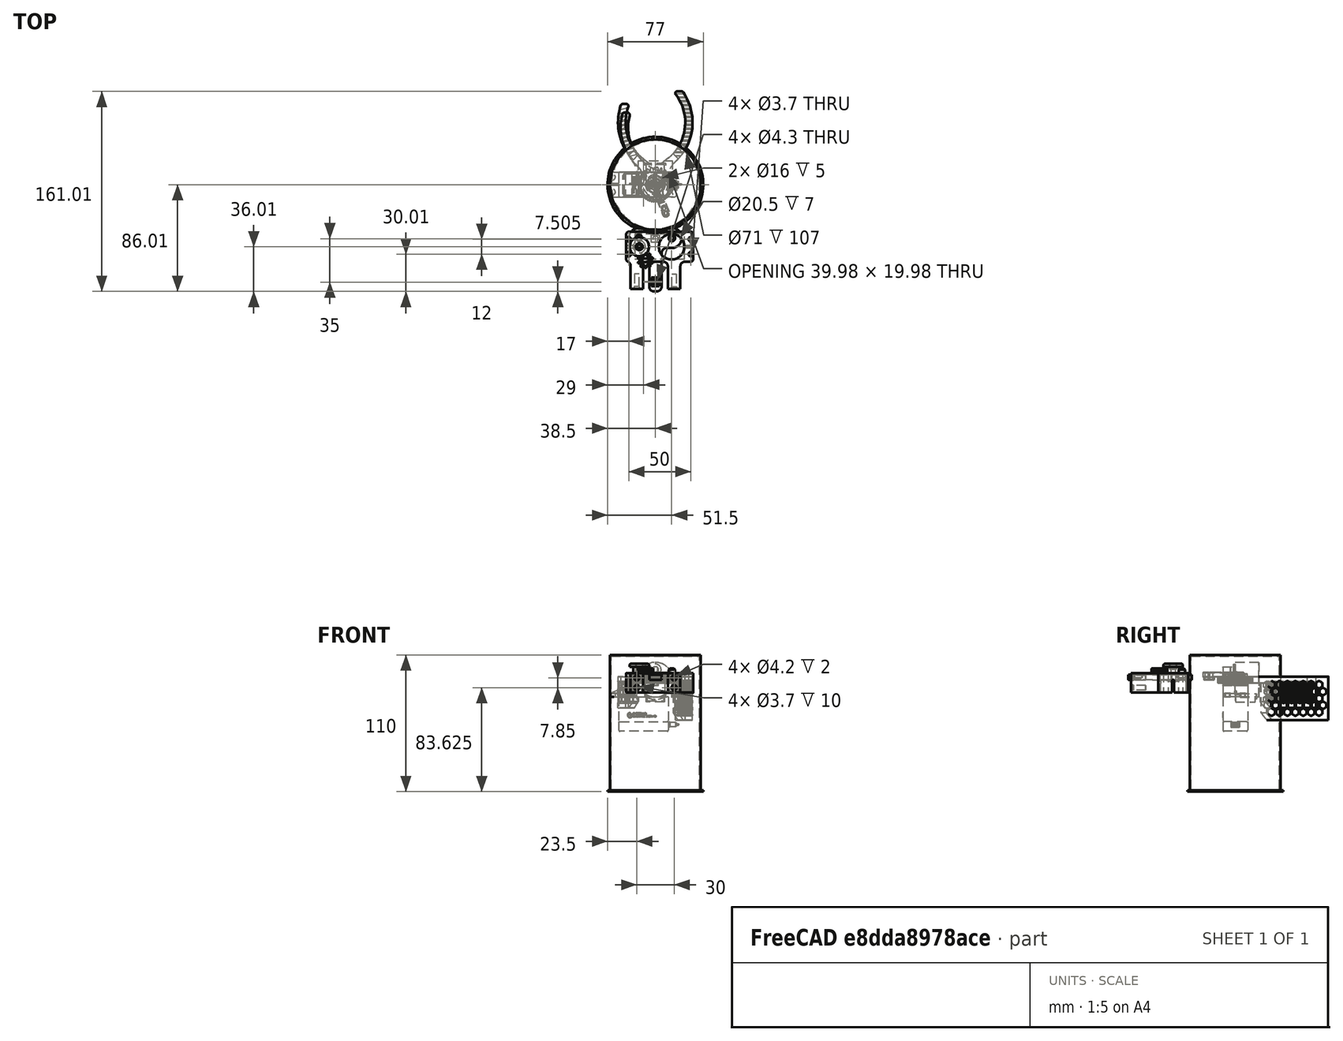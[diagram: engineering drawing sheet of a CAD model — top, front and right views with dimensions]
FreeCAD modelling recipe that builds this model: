
FCSTD DOCUMENT  (FreeCAD 1.0R39109 (Git))
Label: CanaPince
License: All rights reserved
LicenseURL: https://en.wikipedia.org/wiki/All_rights_reserved
objects: Sketcher::SketchObject×43, PartDesign::Pad×25, PartDesign::Pocket×20, PartDesign::CoordinateSystem×15, PartDesign::Body×12, PartDesign::Fillet×10, App::Part×8, PartDesign::Chamfer×6, Part::Part2DObjectPython×5, PartDesign::Mirrored×4, Part::Feature×3, Part::FeaturePython×3, PartDesign::Revolution×3, PartDesign::Line×2, Part::Cut×2, PartDesign::Plane×1, PartDesign::PolarPattern×1, Mesh::Feature×1, PartDesign::MultiTransform×1, App::VarSet×1
note: 333 computed .brp shape members not serialized (recipe doc carries the construction recipe); baked Part::Feature solids carry a one-line shape summary decoded from their .brp

FEATURE [Sketcher::SketchObject] Sketch
  ArcFitTolerance = 0
  AttachmentSupport = -> [XY_Plane]
  FullyConstrained = true
  MakeInternals = false
  MapMode = 5
  sketch-geometry (8):
    g0: ArcOfCircle CenterX=0 CenterY=0 CenterZ=0 NormalX=0 NormalY=0 NormalZ=1 AngleXU=0 Radius=37 StartAngle=4.41351 EndAngle=5.01126
    g1: ArcOfCircle CenterX=-13.25 CenterY=-43.0051 CenterZ=0 NormalX=0 NormalY=0 NormalZ=1 AngleXU=0 Radius=8 StartAngle=1.27192 EndAngle=4.71239
    g2: ArcOfCircle CenterX=13.25 CenterY=-43.0051 CenterZ=0 NormalX=0 NormalY=0 NormalZ=1 AngleXU=0 Radius=8 StartAngle=4.71239 EndAngle=8.15286
    g3: LineSegment StartX=-13.25 StartY=-51.0051 StartZ=0 EndX=-5 EndY=-51.0051 EndZ=0
    g4: LineSegment StartX=13.25 StartY=-51.0051 StartZ=0 EndX=5 EndY=-51.0051 EndZ=0
    g5: LineSegment StartX=-5 StartY=-51.0051 StartZ=0 EndX=-5 EndY=-86.0051 EndZ=0
    g6: LineSegment StartX=5 StartY=-51.0051 StartZ=0 EndX=5 EndY=-86.0051 EndZ=0
    g7: LineSegment StartX=-5 StartY=-86.0051 StartZ=0 EndX=5 EndY=-86.0051 EndZ=0
  constraints (24):
    c: Coincident(g0,g-1)
    c: Radius(g0) = 37
    c: Horizontal(g0,g0)
    c: Radius(g1) = 8
    c: Tangent(g1,g0) = 1.5708
    c: Radius(g2) = 8
    c: Distance(g1,g2) = 26.5
    c: Vertical(g1,g1)
    c: Vertical(g2,g2)
    c: Tangent(g2,g0) = 1.5708
    c: Coincident(g3,g1)
    c: Horizontal(g3)
    c: Coincident(g4,g2)
    c: Horizontal(g4)
    c: Equal(g3,g4)
    c: Distance(g3,g4) = 10
    c: Coincident(g5,g3)
    c: Vertical(g5)
    c: Distance(g5) = 35
    c: Coincident(g6,g4)
    c: Vertical(g6)
    c: Equal(g5,g6)
    c: Coincident(g7,g5)
    c: Coincident(g7,g6)
FEATURE [PartDesign::Pad] Pad
  Direction = (0,0,1)
  Length = 4
  Length2 = 10
  Profile = -> Sketch
  ReferenceAxis = -> Sketch [N_Axis]
  Suppressed = false
  Type = 0
FEATURE [Sketcher::SketchObject] Sketch001
  ArcFitTolerance = 0
  AttachmentSupport = -> [Pad]
  ExternalGeometry = -> [Pad]
  FullyConstrained = true
  MakeInternals = false
  MapMode = 5
  Placement = pos=(0,0,4) rot=(0,0,1;0rad)
  sketch-geometry (2):
    g0: Circle CenterX=-13.25 CenterY=-43.0051 CenterZ=0 NormalX=0 NormalY=0 NormalZ=1 AngleXU=0 Radius=2.6
    g1: Circle CenterX=13.25 CenterY=-43.0051 CenterZ=0 NormalX=0 NormalY=0 NormalZ=1 AngleXU=0 Radius=2.6
  constraints (4):
    c: Coincident(g0,g-3)
    c: Diameter(g0) = 5.2
    c: Coincident(g1,g-4)
    c: Equal(g1,g0)
FEATURE [PartDesign::Pad] Pad001
  BaseFeature = -> Pad
  Direction = (0,0,1)
  Length = 5
  Length2 = 10
  Profile = -> Sketch001
  ReferenceAxis = -> Sketch001 [N_Axis]
  Suppressed = false
  Type = 0
FEATURE [Sketcher::SketchObject] Sketch002
  ArcFitTolerance = 0
  AttachmentSupport = -> [Pad001]
  ExternalGeometry = -> [Pad001]
  FullyConstrained = true
  MakeInternals = false
  MapMode = 5
  Placement = pos=(0,0,4) rot=(0,0,1;0rad)
  sketch-geometry (2):
    g0: Circle CenterX=0 CenterY=-43.5051 CenterZ=0 NormalX=0 NormalY=0 NormalZ=1 AngleXU=0 Radius=2.15
    g1: Circle CenterX=0 CenterY=-78.0051 CenterZ=0 NormalX=0 NormalY=0 NormalZ=1 AngleXU=0 Radius=2.15
  constraints (6):
    c: PointOnObject(g0,g-2)
    c: Diameter(g0) = 4.3
    c: PointOnObject(g1,g-2)
    c: Equal(g0,g1)
    c: Distance(g0,g1) = 34.5
    c: Distance(g0,g-3) = 7.5
FEATURE [PartDesign::Pocket] Pocket
  BaseFeature = -> Pad001
  Direction = (0,0,-1)
  Length = 5
  Length2 = 5
  Profile = -> Sketch002
  ReferenceAxis = -> Sketch002 [N_Axis]
  Suppressed = false
  Type = 1
FEATURE [Sketcher::SketchObject] Sketch003
  ArcFitTolerance = 0
  AttachmentSupport = -> [Pocket]
  ExternalGeometry = -> [Pocket]
  FullyConstrained = true
  MakeInternals = false
  MapMode = 5
  Placement = pos=(0,0,4) rot=(0,0,1;0rad)
  sketch-geometry (10):
    g0: LineSegment StartX=-3.15 StartY=-46.6551 StartZ=0 EndX=-3.15 EndY=-40.3551 EndZ=0
    g1: LineSegment StartX=-3.15 StartY=-40.3551 StartZ=0 EndX=3.15 EndY=-40.3551 EndZ=0
    g2: LineSegment StartX=3.15 StartY=-40.3551 StartZ=0 EndX=3.15 EndY=-46.6551 EndZ=0
    g3: LineSegment StartX=3.15 StartY=-46.6551 StartZ=0 EndX=-3.15 EndY=-46.6551 EndZ=0
    g4: GeomPoint [constr] X=0 Y=-43.5051 Z=0
    g5: LineSegment StartX=-3.15 StartY=-81.1551 StartZ=0 EndX=-3.15 EndY=-74.8551 EndZ=0
    g6: LineSegment StartX=-3.15 StartY=-74.8551 StartZ=0 EndX=3.15 EndY=-74.8551 EndZ=0
    g7: LineSegment StartX=3.15 StartY=-74.8551 StartZ=0 EndX=3.15 EndY=-81.1551 EndZ=0
    g8: LineSegment StartX=3.15 StartY=-81.1551 StartZ=0 EndX=-3.15 EndY=-81.1551 EndZ=0
    g9: GeomPoint [constr] X=0 Y=-78.0051 Z=0
  constraints (24):
    c: Coincident(g0,g1)
    c: Coincident(g1,g2)
    c: Coincident(g2,g3)
    c: Coincident(g3,g0)
    c: Horizontal(g1)
    c: Horizontal(g3)
    c: Vertical(g0)
    c: Vertical(g2)
    c: Symmetric(g1,g0,g4)
    c: Coincident(g4,g-3)
    c: Distance(g1) = 6.3
    c: Equal(g1,g2)
    c: Coincident(g5,g6)
    c: Coincident(g6,g7)
    c: Coincident(g7,g8)
    c: Coincident(g8,g5)
    c: Horizontal(g6)
    c: Horizontal(g8)
    c: Vertical(g5)
    c: Vertical(g7)
    c: Symmetric(g6,g5,g9)
    c: Coincident(g9,g-4)
    c: Equal(g3,g6)
    c: Equal(g6,g7)
FEATURE [PartDesign::Pocket] Pocket001
  BaseFeature = -> Pocket
  Direction = (0,0,-1)
  Length = 2.5
  Length2 = 5
  Profile = -> Sketch003
  ReferenceAxis = -> Sketch003 [N_Axis]
  Suppressed = false
  Type = 0
FEATURE [PartDesign::Fillet] Fillet
  Base = -> Pocket001 [Edge34,Edge33,Edge35,Edge36]
  BaseFeature = -> Pocket001
  Radius = 4
  SupportTransform = false
  Suppressed = false
  UseAllEdges = false
FEATURE [PartDesign::Chamfer] Chamfer
  Angle = 45
  Base = -> Fillet [Edge66,Edge72]
  BaseFeature = -> Fillet
  ChamferType = 0
  FlipDirection = false
  Size = 1
  Size2 = 1
  SupportTransform = false
  Suppressed = false
  UseAllEdges = false
FEATURE [Sketcher::SketchObject] Sketch004
  ArcFitTolerance = 0
  AttachmentSupport = -> [Chamfer]
  ExternalGeometry = -> [Chamfer]
  FullyConstrained = true
  MakeInternals = false
  MapMode = 5
  Placement = pos=(0,0,4) rot=(0,0,1;0rad)
  sketch-geometry (1):
    g0: Circle CenterX=-7 CenterY=-60.7551 CenterZ=0 NormalX=0 NormalY=0 NormalZ=1 AngleXU=0 Radius=4.65
  constraints (3):
    c: Diameter(g0) = 9.3
    c: Distance(g0,g-3) = 2
    c: DistanceY(g0,g-4) = 17.25
FEATURE [PartDesign::Pocket] Pocket002
  BaseFeature = -> Chamfer
  Direction = (0,0,-1)
  Length = 5
  Length2 = 5
  Profile = -> Sketch004
  ReferenceAxis = -> Sketch004 [N_Axis]
  Suppressed = false
  Type = 1
FEATURE [PartDesign::Fillet] Fillet001
  Base = -> Pocket002 [Edge55,Edge52]
  BaseFeature = -> Pocket002
  Radius = 3
  SupportTransform = false
  Suppressed = false
  UseAllEdges = false
FEATURE [PartDesign::CoordinateSystem] LCS_1
  AttacherType = Attacher::AttachEngine3D
  AttachmentSupport = -> [Fillet001]
  MapMode = 11
  Placement = pos=(0,-43.5051,1.5) rot=(0,0,1;1.5708rad)
FEATURE [PartDesign::CoordinateSystem] LCS_2
  AttacherType = Attacher::AttachEngine3D
  AttachmentSupport = -> [Fillet001]
  MapMode = 11
  Placement = pos=(0,-78.0051,1.5) rot=(0,0,1;1.5708rad)
FEATURE [PartDesign::CoordinateSystem] LCS_3
  AttacherType = Attacher::AttachEngine3D
  AttachmentSupport = -> [Fillet001]
  MapMode = 11
  Placement = pos=(13.25,-43.0051,8) rot=(0,0,1;1.5708rad)
FEATURE [PartDesign::CoordinateSystem] LCS_4
  AttacherType = Attacher::AttachEngine3D
  AttachmentSupport = -> [Fillet001]
  MapMode = 11
  Placement = pos=(-13.25,-43.0051,8) rot=(0,0,1;1.5708rad)
FEATURE [PartDesign::Body] Body  label="partie_fixe_V1"
  AllowCompound = false
  Group = -> [Sketch,Pad,Sketch001,Pad001,Sketch002,Pocket,Sketch003,Pocket001,Fillet,Chamfer,Sketch004,Pocket002,Fillet001,LCS_1,LCS_2,LCS_3,LCS_4]
  Origin = -> Origin
  Tip = -> Fillet001
FEATURE [Part::Part2DObjectPython] InvoluteGear  # Draft 2D object (typed FeaturePython)
  AddendumCoefficient = 1
  DedendumCoefficient = 1.25
  ExternalGear = true
  HighPrecision = true
  Modules = 1
  NumberOfTeeth = 26
  Placement = pos=(-15,-46,0) rot=(0,0,20;0rad)
  PressureAngle = 20
  ProfileShiftCoefficient = 0
  RootFilletCoefficient = 0.38
FEATURE [Sketcher::SketchObject] Sketch005
  ArcFitTolerance = 0
  AttachmentSupport = -> [XY_Plane001]
  FullyConstrained = true
  MakeInternals = false
  MapMode = 5
  sketch-geometry (5):
    g0: ArcOfCircle CenterX=0 CenterY=0 CenterZ=0 NormalX=0 NormalY=0 NormalZ=1 AngleXU=0 Radius=37 StartAngle=2.8113 EndAngle=4.39717
    g1: Circle CenterX=-15 CenterY=-46 CenterZ=0 NormalX=0 NormalY=0 NormalZ=1 AngleXU=0 Radius=8
    g2: ArcOfCircle CenterX=-15 CenterY=-46 CenterZ=0 NormalX=0 NormalY=0 NormalZ=1 AngleXU=0 Radius=11.3839 StartAngle=2.22683 EndAngle=7.53877
    g3: ArcOfCircle CenterX=0 CenterY=0 CenterZ=0 NormalX=0 NormalY=0 NormalZ=1 AngleXU=0 Radius=43 StartAngle=2.85877 EndAngle=4.17683
    g4: LineSegment StartX=-41.2916 StartY=12 StartZ=0 EndX=-35 EndY=12 EndZ=0
  constraints (14):
    c: Coincident(g0,g-1)
    c: Radius(g0) = 37
    c: Distance(g0,g-2) = 35
    c: Diameter(g1) = 16
    c: Distance(g1,g-2) = 15
    c: Coincident(g2,g1)
    c: Tangent(g2,g0) = 1.5708
    c: Coincident(g3,g0)
    c: Coincident(g2,g3)
    c: Radius(g3) = 43
    c: Coincident(g4,g3)
    c: Coincident(g4,g0)
    c: Horizontal(g4)
    c: Distance(g1,g-1) = 46
FEATURE [PartDesign::Pad] Pad002
  Direction = (0,0,1)
  Length = 5
  Length2 = 10
  Midplane = true
  Profile = -> Sketch005
  ReferenceAxis = -> Sketch005 [N_Axis]
  Suppressed = false
  Type = 0
FEATURE [PartDesign::Fillet] Fillet002
  Base = -> Pad002 [Edge8]
  BaseFeature = -> Pad002
  Radius = 10
  SupportTransform = false
  Suppressed = false
  UseAllEdges = false
FEATURE [PartDesign::Fillet] Fillet003
  Base = -> Fillet002 [Edge17,Edge12]
  BaseFeature = -> Fillet002
  Radius = 2
  SupportTransform = false
  Suppressed = false
  UseAllEdges = false
FEATURE [PartDesign::Chamfer] Chamfer001
  Angle = 45
  Base = -> Fillet003 [Edge24,Edge8]
  BaseFeature = -> Fillet003
  ChamferType = 0
  FlipDirection = false
  Size = 0.8
  Size2 = 1
  SupportTransform = false
  Suppressed = false
  UseAllEdges = false
FEATURE [PartDesign::Line] DatumLine
  AttacherType = Attacher::AttachEngineLine
  AttachmentSupport = -> [Chamfer001]
  Length = 20
  MapMode = 42
  Placement = pos=(-15,-46,-1e-16) rot=(0,0,1;0rad)
  ResizeMode = 0
FEATURE [PartDesign::Pad] Pad003
  BaseFeature = -> Chamfer001
  Direction = (0,0,1)
  Length = 5
  Length2 = 10
  Midplane = true
  Profile = -> InvoluteGear
  ReferenceAxis = -> InvoluteGear [N_Axis]
  Suppressed = false
  Type = 0
FEATURE [Sketcher::SketchObject] Sketch006
  ArcFitTolerance = 0
  AttachmentSupport = -> [Pad003]
  FullyConstrained = false
  MakeInternals = false
  MapMode = 5
  Placement = pos=(0,0,2.5) rot=(0,0,1;0rad)
  sketch-geometry (1):
    g0: Circle CenterX=-15 CenterY=-46 CenterZ=0 NormalX=0 NormalY=0 NormalZ=1 AngleXU=0 Radius=8
  constraints (1):
    c: Diameter(g0) = 16
FEATURE [PartDesign::Pocket] Pocket003
  BaseFeature = -> Pad003
  Direction = (0,0,-1)
  Length = 5
  Length2 = 5
  Profile = -> Sketch006
  ReferenceAxis = -> Sketch006 [N_Axis]
  Suppressed = false
  Type = 1
FEATURE [Sketcher::SketchObject] Sketch007
  ArcFitTolerance = 0
  AttachmentSupport = -> [Pocket003]
  ExternalGeometry = -> [Pocket003]
  FullyConstrained = true
  MakeInternals = false
  MapMode = 5
  Placement = pos=(0,0,2.5) rot=(0,0,1;0rad)
  sketch-geometry (4):
    g0: ArcOfCircle CenterX=-15 CenterY=-46 CenterZ=0 NormalX=0 NormalY=0 NormalZ=1 AngleXU=0 Radius=11.5 StartAngle=0.593412 EndAngle=1.25558
    g1: ArcOfCircle CenterX=-15 CenterY=-46 CenterZ=0 NormalX=0 NormalY=0 NormalZ=1 AngleXU=0 Radius=15 StartAngle=0.593412 EndAngle=1.84626
    g2: LineSegment StartX=-5.46607 StartY=-39.5693 StartZ=0 EndX=-2.56444 EndY=-37.6121 EndZ=0
    g3: ArcOfCircle CenterX=0 CenterY=0 CenterZ=0 NormalX=0 NormalY=0 NormalZ=1 AngleXU=0 Radius=36.8839 StartAngle=4.1687 EndAngle=4.39717
  constraints (11):
    c: Coincident(g0,g-3)
    c: Coincident(g1,g0)
    c: Coincident(g2,g0)
    c: Coincident(g2,g1)
    c: Coincident(g1,g3)
    c: Tangent(g3,g0) = 1.5708
    c: Perpendicular(g0,g2)
    c: Radius(g0) = 11.5
    c: Coincident(g3,g-1)
    c: Radius(g1) = 15
    c: Angle(g-1,g2) = 0.593412
FEATURE [PartDesign::Pocket] Pocket004
  BaseFeature = -> Pocket003
  Direction = (0,0,-1)
  Length = 5
  Length2 = 5
  Profile = -> Sketch007
  ReferenceAxis = -> Sketch007 [N_Axis]
  Suppressed = false
  Type = 0
FEATURE [PartDesign::CoordinateSystem] LCS_005
  AttacherType = Attacher::AttachEngine3D
  AttachmentSupport = -> [Pocket004]
  MapMode = 11
  Placement = pos=(-15,-46,2.5) rot=(0,0,1;1.5708rad)
FEATURE [PartDesign::Body] Body001  label="bras_R"
  AllowCompound = false
  Group = -> [Sketch005,Pad002,Fillet002,Fillet003,Chamfer001,DatumLine,InvoluteGear,Pad003,Sketch006,Pocket003,Sketch007,Pocket004,LCS_005]
  Origin = -> Origin001
  Placement = pos=(15,46,0) rot=(0,0,1;0rad)
  Tip = -> Pocket004
FEATURE [Part::Part2DObjectPython] InvoluteGear001  # Draft 2D object (typed FeaturePython)
  AddendumCoefficient = 1
  DedendumCoefficient = 1.25
  ExternalGear = true
  HighPrecision = true
  Modules = 1.05
  NumberOfTeeth = 10
  PressureAngle = 20
  ProfileShiftCoefficient = 0
  RootFilletCoefficient = 0.38
FEATURE [PartDesign::Pad] Pad004
  Direction = (0,0,1)
  Length = 4
  Length2 = 10
  Profile = -> InvoluteGear001
  ReferenceAxis = -> InvoluteGear001 [N_Axis]
  Suppressed = false
  Type = 0
FEATURE [Sketcher::SketchObject] Sketch008
  ArcFitTolerance = 0
  AttachmentSupport = -> [XY_Plane002]
  FullyConstrained = true
  MakeInternals = false
  MapMode = 5
  sketch-geometry (1):
    g0: Circle CenterX=0 CenterY=0 CenterZ=0 NormalX=0 NormalY=0 NormalZ=1 AngleXU=0 Radius=6.5
  constraints (2):
    c: Coincident(g0,g-1)
    c: Diameter(g0) = 13
FEATURE [Sketcher::SketchObject] Sketch009
  ArcFitTolerance = 0
  AttachmentSupport = -> [Pad004]
  FullyConstrained = true
  MakeInternals = false
  MapMode = 5
  Placement = pos=(0,0,4) rot=(0,0,1;0rad)
  sketch-geometry (5):
    g0: LineSegment StartX=-1.5 StartY=-2.5 StartZ=0 EndX=-1.5 EndY=2.5 EndZ=0
    g1: LineSegment StartX=-1.5 StartY=2.5 StartZ=0 EndX=1.5 EndY=2.5 EndZ=0
    g2: LineSegment StartX=1.5 StartY=2.5 StartZ=0 EndX=1.5 EndY=-2.5 EndZ=0
    g3: LineSegment StartX=1.5 StartY=-2.5 StartZ=0 EndX=-1.5 EndY=-2.5 EndZ=0
    g4: GeomPoint [constr] X=0 Y=0 Z=0
  constraints (12):
    c: Coincident(g0,g1)
    c: Coincident(g1,g2)
    c: Coincident(g2,g3)
    c: Coincident(g3,g0)
    c: Horizontal(g1)
    c: Horizontal(g3)
    c: Vertical(g0)
    c: Vertical(g2)
    c: Symmetric(g1,g0,g4)
    c: Coincident(g4,g-1)
    c: Distance(g2) = 5
    c: Distance(g1) = 3
FEATURE [PartDesign::Pocket] Pocket005
  BaseFeature = -> Pad004
  Direction = (0,0,-1)
  Length = 5
  Length2 = 5
  Profile = -> Sketch009
  ReferenceAxis = -> Sketch009 [N_Axis]
  Suppressed = false
  Type = 1
FEATURE [PartDesign::Fillet] Fillet004
  Base = -> Pocket005 [Edge310,Edge311,Edge312,Edge309]
  BaseFeature = -> Pocket005
  Radius = 0.8
  SupportTransform = false
  Suppressed = false
  UseAllEdges = false
FEATURE [PartDesign::CoordinateSystem] LCS_006
  AttacherType = Attacher::AttachEngine3D
  AttachmentSupport = -> [Fillet004]
  MapMode = 5
  Placement = pos=(0,0,4) rot=(0,0,1;0rad)
FEATURE [PartDesign::Body] Body002  label="pignon"
  AllowCompound = false
  Group = -> [Sketch008,InvoluteGear001,Pad004,Sketch009,Pocket005,Fillet004,LCS_006]
  Origin = -> Origin002
  Placement = pos=(-8,-61,5) rot=(0,0,1;4.71239rad)
  Tip = -> Fillet004
FEATURE [Sketcher::SketchObject] Sketch010
  ArcFitTolerance = 0
  AttachmentSupport = -> [XZ_Plane004]
  FullyConstrained = true
  MakeInternals = false
  MapMode = 5
  Placement = pos=(0,0,0) rot=(1,0,0;1.5708rad)
  sketch-geometry (1):
    g0: Circle CenterX=0 CenterY=0 CenterZ=0 NormalX=0 NormalY=0 NormalZ=1 AngleXU=0 Radius=14
  constraints (2):
    c: Coincident(g0,g-1)
    c: Diameter(g0) = 28
FEATURE [PartDesign::Pad] Pad005
  Direction = (0,-1,2e-16)
  Length = 19
  Length2 = 100
  Placement = pos=(0,0,0) rot=(1,0,0;1.5708rad)
  Profile = -> Sketch010
  ReferenceAxis = -> Sketch010 [N_Axis]
  Reversed = true
  Suppressed = false
  Type = 0
FEATURE [Sketcher::SketchObject] Sketch011
  ArcFitTolerance = 0
  AttachmentSupport = -> [Pad005]
  ExternalGeometry = -> [Pad005]
  FullyConstrained = true
  MakeInternals = false
  MapMode = 5
  Placement = pos=(0,0,0) rot=(1,0,0;1.5708rad)
  sketch-geometry (4):
    g0: LineSegment StartX=-7.25 StartY=-11.9765 StartZ=0 EndX=7.25 EndY=-11.9765 EndZ=0
    g1: LineSegment StartX=7.25 StartY=-11.9765 StartZ=0 EndX=7.25 EndY=-18 EndZ=0
    g2: LineSegment StartX=7.25 StartY=-18 StartZ=0 EndX=-7.25 EndY=-18 EndZ=0
    g3: LineSegment StartX=-7.25 StartY=-18 StartZ=0 EndX=-7.25 EndY=-11.9765 EndZ=0
  constraints (11):
    c: Coincident(g0,g1)
    c: Coincident(g1,g2)
    c: Coincident(g2,g3)
    c: Coincident(g3,g0)
    c: Horizontal(g0)
    c: Vertical(g1)
    c: Vertical(g3)
    c: PointOnObject(g0,g-3)
    c: Symmetric(g2,g1,g-2)
    c: DistanceX(g2,g2) = 14.5
    c: DistanceY(g1,g-1) = 18
FEATURE [PartDesign::Pad] Pad006
  BaseFeature = -> Pad005
  Direction = (0,-1,2e-16)
  Length = 16
  Length2 = 100
  Placement = pos=(0,0,0) rot=(1,0,0;1.5708rad)
  Profile = -> Sketch011
  ReferenceAxis = -> Sketch011 [N_Axis]
  Refine = true
  Reversed = true
  Suppressed = false
  Type = 0
FEATURE [Sketcher::SketchObject] Sketch012
  ArcFitTolerance = 0
  AttachmentSupport = -> [Pad006]
  ExternalGeometry = -> [Pad006]
  FullyConstrained = true
  MakeInternals = false
  MapMode = 5
  Placement = pos=(0,0,0) rot=(1,0,0;1.5708rad)
  sketch-geometry (5):
    g0: Circle CenterX=-17.5 CenterY=-1e-16 CenterZ=0 NormalX=0 NormalY=0 NormalZ=1 AngleXU=0 Radius=2.1
    g1: ArcOfCircle CenterX=-17.5 CenterY=-1e-16 CenterZ=0 NormalX=0 NormalY=0 NormalZ=1 AngleXU=0 Radius=3.5 StartAngle=1.5708 EndAngle=4.71239
    g2: LineSegment StartX=-17.5 StartY=3.5 StartZ=0 EndX=-13.5554 EndY=3.5 EndZ=0
    g3: LineSegment StartX=-13.5554 StartY=3.5 StartZ=0 EndX=-13.5554 EndY=-3.5 EndZ=0
    g4: LineSegment StartX=-13.5554 StartY=-3.5 StartZ=0 EndX=-17.5 EndY=-3.5 EndZ=0
  constraints (14):
    c: Coincident(g1,g0)
    c: Symmetric(g1,g1,g-1)
    c: Vertical(g1,g0)
    c: Coincident(g2,g1)
    c: Horizontal(g2)
    c: Coincident(g3,g2)
    c: Vertical(g3)
    c: Coincident(g4,g3)
    c: Coincident(g4,g1)
    c: Horizontal(g4)
    c: PointOnObject(g2,g-3)
    c: Diameter(g0) = 4.2
    c: Radius(g1) = 3.5
    c: DistanceX(g0,g-1) = 17.5
FEATURE [PartDesign::Pad] Pad007
  BaseFeature = -> Pad006
  Direction = (0,-1,2e-16)
  Length = 0.8
  Length2 = 100
  Placement = pos=(0,0,0) rot=(1,0,0;1.5708rad)
  Profile = -> Sketch012
  ReferenceAxis = -> Sketch012 [N_Axis]
  Refine = true
  Reversed = true
  Suppressed = false
  Type = 0
FEATURE [PartDesign::Mirrored] Mirrored
  BaseFeature = -> Pad007
  MirrorPlane = -> Sketch012 [V_Axis]
  Originals = -> [Pad007]
  Placement = pos=(0,0,0) rot=(1,0,0;1.5708rad)
  Refine = true
  Suppressed = false
  TransformMode = 0
FEATURE [Sketcher::SketchObject] Sketch013
  ArcFitTolerance = 0
  AttachmentSupport = -> [Mirrored]
  FullyConstrained = true
  MakeInternals = false
  MapMode = 5
  Placement = pos=(0,0,0) rot=(1,0,0;1.5708rad)
  sketch-geometry (1):
    g0: Circle CenterX=0 CenterY=8 CenterZ=0 NormalX=0 NormalY=0 NormalZ=1 AngleXU=0 Radius=4.6
  constraints (3):
    c: PointOnObject(g0,g-2)
    c: Diameter(g0) = 9.2
    c: DistanceY(g-1,g0) = 8
FEATURE [PartDesign::Pad] Pad008
  BaseFeature = -> Mirrored
  Direction = (0,-1,2e-16)
  Length = 1.5
  Length2 = 100
  Placement = pos=(0,0,0) rot=(1,0,0;1.5708rad)
  Profile = -> Sketch013
  ReferenceAxis = -> Sketch013 [N_Axis]
  Suppressed = false
  Type = 0
FEATURE [Sketcher::SketchObject] Sketch014
  ArcFitTolerance = 0
  AttachmentSupport = -> [Pad008]
  ExternalGeometry = -> [Pad008]
  FullyConstrained = true
  MakeInternals = false
  MapMode = 5
  Placement = pos=(0,-1.5,0) rot=(1,0,0;1.5708rad)
  sketch-geometry (1):
    g0: Circle CenterX=0 CenterY=8 CenterZ=0 NormalX=0 NormalY=0 NormalZ=1 AngleXU=0 Radius=2.5
  constraints (2):
    c: Coincident(g0,g-3)
    c: Diameter(g0) = 5
FEATURE [PartDesign::Pad] Pad009
  BaseFeature = -> Pad008
  Direction = (0,-1,2e-16)
  Length = 2.5
  Length2 = 100
  Placement = pos=(0,0,0) rot=(1,0,0;1.5708rad)
  Profile = -> Sketch014
  ReferenceAxis = -> Sketch014 [N_Axis]
  Suppressed = false
  Type = 0
FEATURE [Sketcher::SketchObject] Sketch015
  ArcFitTolerance = 0
  AttachmentSupport = -> [Pad009]
  ExternalGeometry = -> [Pad009]
  FullyConstrained = true
  MakeInternals = false
  MapMode = 5
  Placement = pos=(0,-4,0) rot=(1,0,0;1.5708rad)
  sketch-geometry (4):
    g0: LineSegment StartX=-1.5 StartY=10 StartZ=0 EndX=-1.5 EndY=6 EndZ=0
    g1: LineSegment StartX=1.5 StartY=10 StartZ=0 EndX=1.5 EndY=6 EndZ=0
    g2: ArcOfCircle CenterX=0 CenterY=8 CenterZ=0 NormalX=0 NormalY=0 NormalZ=1 AngleXU=0 Radius=2.5 StartAngle=0.927295 EndAngle=2.2143
    g3: ArcOfCircle CenterX=0 CenterY=8 CenterZ=0 NormalX=0 NormalY=0 NormalZ=1 AngleXU=0 Radius=2.5 StartAngle=4.06889 EndAngle=5.35589
  constraints (12):
    c: PointOnObject(g0,g-3)
    c: PointOnObject(g0,g-3)
    c: Vertical(g0)
    c: Vertical(g1)
    c: Coincident(g2,g-3)
    c: Coincident(g2,g0)
    c: Coincident(g2,g1)
    c: Coincident(g3,g2)
    c: Coincident(g3,g0)
    c: Coincident(g3,g1)
    c: DistanceX(g0,g1) = 3
    c: Horizontal(g0,g1)
FEATURE [PartDesign::Pad] Pad010
  BaseFeature = -> Pad009
  Direction = (0,-1,2e-16)
  Length = 6
  Length2 = 100
  Placement = pos=(0,0,0) rot=(1,0,0;1.5708rad)
  Profile = -> Sketch015
  ReferenceAxis = -> Sketch015 [N_Axis]
  Refine = true
  Suppressed = false
  Type = 0
FEATURE [PartDesign::Plane] DatumPlane
  AttachmentOffset = pos=(0,0,-4) rot=(0,0,1;0rad)
  AttachmentSupport = -> [Pad010]
  Length = 60
  MapMode = 2
  Placement = pos=(0,4,-9e-16) rot=(1,0,0;1.5708rad)
  ResizeMode = 0
  Width = 60
FEATURE [Sketcher::SketchObject] Sketch016
  ArcFitTolerance = 0
  AttachmentSupport = -> [DatumPlane]
  ExternalGeometry = -> [Pad010]
  FullyConstrained = true
  MakeInternals = false
  MapMode = 5
  Placement = pos=(0,4,-9e-16) rot=(1,0,0;1.5708rad)
  sketch-geometry (4):
    g0: ArcOfCircle CenterX=0 CenterY=0 CenterZ=0 NormalX=0 NormalY=0 NormalZ=1 AngleXU=0 Radius=15.7659 StartAngle=4.14297 EndAngle=4.23456
    g1: LineSegment StartX=-7.25 StartY=-14 StartZ=0 EndX=-7.25 EndY=-11.9765 EndZ=0
    g2: LineSegment StartX=-8.5 StartY=-13.2783 StartZ=0 EndX=-8.5 EndY=-11.1243 EndZ=0
    g3: ArcOfCircle CenterX=0 CenterY=0 CenterZ=0 NormalX=0 NormalY=0 NormalZ=1 AngleXU=0 Radius=14 StartAngle=4.05993 EndAngle=4.16804
  constraints (11):
    c: Coincident(g0,g-1)
    c: Coincident(g1,g-4)
    c: Coincident(g2,g0)
    c: Vertical(g2)
    c: Coincident(g3,g0)
    c: Coincident(g3,g1)
    c: Coincident(g3,g2)
    c: Coincident(g1,g0)
    c: DistanceX(g2,g0) = 8.5
    c: Vertical(g1)
    c: DistanceY(g-3,g0) = 4
FEATURE [PartDesign::Pad] Pad011
  BaseFeature = -> Pad010
  Direction = (0,-1,2e-16)
  Length = 10
  Length2 = 100
  Placement = pos=(0,0,0) rot=(1,0,0;1.5708rad)
  Profile = -> Sketch016
  ReferenceAxis = -> Sketch016 [N_Axis]
  Refine = true
  Suppressed = false
  Type = 3
  UpToFace = -> Pad010 [Face11]
FEATURE [PartDesign::Mirrored] Mirrored001
  BaseFeature = -> Pad011
  MirrorPlane = -> Sketch016 [V_Axis]
  Originals = -> [Pad011]
  Placement = pos=(0,0,0) rot=(1,0,0;1.5708rad)
  Refine = true
  Suppressed = false
  TransformMode = 0
FEATURE [Sketcher::SketchObject] Sketch017
  ArcFitTolerance = 0
  AttachmentSupport = -> [Mirrored001]
  ExternalGeometry = -> [Mirrored001]
  FullyConstrained = true
  MakeInternals = false
  MapMode = 5
  Placement = pos=(0,16,0) rot=(-1,0,0;1.5708rad)
  sketch-geometry (4):
    g0: ArcOfCircle CenterX=0 CenterY=0 CenterZ=0 NormalX=0 NormalY=0 NormalZ=1 AngleXU=0 Radius=14 StartAngle=0.918336 EndAngle=2.22326
    g1: ArcOfCircle CenterX=0 CenterY=0 CenterZ=0 NormalX=0 NormalY=0 NormalZ=1 AngleXU=0 Radius=15.7659 StartAngle=1.00138 EndAngle=2.14021
    g2: LineSegment StartX=-8.5 StartY=13.2783 StartZ=0 EndX=-8.5 EndY=11.1243 EndZ=0
    g3: LineSegment StartX=8.5 StartY=13.2783 StartZ=0 EndX=8.5 EndY=11.1243 EndZ=0
  constraints (10):
    c: Coincident(g0,g-1)
    c: Coincident(g0,g-3)
    c: Coincident(g1,g0)
    c: Coincident(g1,g-4)
    c: Coincident(g2,g1)
    c: Coincident(g2,g0)
    c: Coincident(g3,g1)
    c: Coincident(g3,g0)
    c: Vertical(g3)
    c: Horizontal(g1,g1)
FEATURE [PartDesign::Pad] Pad012
  BaseFeature = -> Mirrored001
  Direction = (0,1,2e-16)
  Length = 1
  Length2 = 100
  Placement = pos=(0,0,0) rot=(1,0,0;1.5708rad)
  Profile = -> Sketch017
  ReferenceAxis = -> Sketch017 [N_Axis]
  Refine = true
  Suppressed = false
  Type = 0
FEATURE [Sketcher::SketchObject] Sketch018
  ArcFitTolerance = 0
  AttachmentSupport = -> [Pad012]
  ExternalGeometry = -> [Pad012]
  FullyConstrained = false
  MakeInternals = false
  MapMode = 5
  Placement = pos=(0,0,0) rot=(1,0,0;1.5708rad)
  sketch-geometry (8):
    g0: LineSegment StartX=-7.25 StartY=-11.9765 StartZ=0 EndX=-7.25 EndY=-18 EndZ=0
    g1: LineSegment StartX=7.25 StartY=-18 StartZ=0 EndX=-7.25 EndY=-18 EndZ=0
    g2: LineSegment StartX=7.25 StartY=-18 StartZ=0 EndX=7.25 EndY=-11.9765 EndZ=0
    g3: ArcOfCircle CenterX=0 CenterY=0 CenterZ=0 NormalX=0 NormalY=0 NormalZ=1 AngleXU=0 Radius=14 StartAngle=4.16804 EndAngle=4.20929
    g4: LineSegment StartX=-6.75 StartY=-12.2653 StartZ=0 EndX=-6.75 EndY=-17 EndZ=0
    g5: LineSegment StartX=-6.75 StartY=-17 StartZ=0 EndX=6.75 EndY=-17 EndZ=0
    g6: LineSegment StartX=6.75 StartY=-17 StartZ=0 EndX=6.75 EndY=-12.2653 EndZ=0
    g7: ArcOfCircle CenterX=-1.15416 CenterY=1.9985 CenterZ=0 NormalX=0 NormalY=0 NormalZ=1 AngleXU=0 Radius=16.3074 StartAngle=5.21841 EndAngle=5.25381
  constraints (19):
    c: Coincident(g0,g-3)
    c: Coincident(g0,g-5)
    c: Coincident(g1,g-6)
    c: Coincident(g1,g0)
    c: Coincident(g2,g1)
    c: Coincident(g2,g-4)
    c: Coincident(g3,g-1)
    c: Coincident(g3,g0)
    c: Coincident(g7,g2)
    c: Vertical(g4)
    c: Coincident(g5,g4)
    c: Horizontal(g5)
    c: Coincident(g6,g5)
    c: Symmetric(g4,g6,g-2)
    c: Vertical(g6)
    c: DistanceX(g0,g4) = 0.5
    c: DistanceY(g0,g4) = 1
    c: Coincident(g3,g4)
    c: Coincident(g7,g6)
FEATURE [PartDesign::Pocket] Pocket006
  BaseFeature = -> Pad012
  Direction = (0,1,-2e-16)
  Length = 0.1
  Length2 = 100
  Placement = pos=(0,0,0) rot=(1,0,0;1.5708rad)
  Profile = -> Sketch018
  Suppressed = false
  Type = 0
FEATURE [PartDesign::Body] Body003  label="28BYJ_48_StepperBody"
  AllowCompound = false
  Group = -> [Sketch010,Pad005,Sketch011,Pad006,Sketch012,Pad007,Mirrored,Sketch013,Pad008,Sketch014,Pad009,Sketch015,Pad010,DatumPlane,Sketch016,Pad011,Mirrored001,Sketch017,Pad012,Sketch018,Pocket006]
  Origin = -> Origin004
  Tip = -> Pocket006
FEATURE [PartDesign::CoordinateSystem] LCS_Mounting_Hole1
  AttacherType = Attacher::AttachEngine3D
  AttachmentSupport = -> [Pocket006]
  MapMode = 11
  Placement = pos=(-17.5,0.8,-1e-16) rot=(0.57735,-0.57735,0.57735;2.0944rad)
FEATURE [PartDesign::CoordinateSystem] LCS_Mounting_Hole2
  AttacherType = Attacher::AttachEngine3D
  AttachmentOffset = pos=(0,0,0) rot=(1,0,0;3.14159rad)
  AttachmentSupport = -> [Pocket006]
  MapMode = 11
  Placement = pos=(17.5,0.8,-1e-16) rot=(-0.57735,0.57735,-0.57735;4.18879rad)
FEATURE [PartDesign::CoordinateSystem] LCS_Mounting_Housing_Center
  AttacherType = Attacher::AttachEngine3D
  AttachmentSupport = -> [Pocket006]
  MapMode = 11
  Placement = pos=(0,0.8,-4e-16) rot=(0.480384,0.620174,-0.620174;2.24593rad)
FEATURE [PartDesign::CoordinateSystem] LCS_Shaft_top_center
  AttacherType = Attacher::AttachEngine3D
  AttachmentOffset = pos=(0,0,8.5) rot=(0,0,1;0rad)
  AttachmentSupport = -> [Pocket006]
  MapMode = 11
  Placement = pos=(0,-10,8) rot=(0.57735,-0.57735,0.57735;2.0944rad)
FEATURE [App::Part] Part  label="28BYJ_48"
  Group = -> [Body003,LCS_Mounting_Housing_Center,LCS_Shaft_top_center,LCS_Mounting_Hole1,LCS_Mounting_Hole2]
  Origin = -> Origin003
  Placement = pos=(-2.03e-14,-61,1.02e-14) rot=(-0.57735,-0.57735,0.57735;2.0944rad)
FEATURE [Part::Part2DObjectPython] InvoluteGear002  # Draft 2D object (typed FeaturePython)
  AddendumCoefficient = 1
  DedendumCoefficient = 1.25
  ExternalGear = true
  HighPrecision = true
  Modules = 1
  NumberOfTeeth = 26
  Placement = pos=(-15,-46,0) rot=(0,0,1;0.122173rad)
  PressureAngle = 20
  ProfileShiftCoefficient = 0
  RootFilletCoefficient = 0.38
FEATURE [Sketcher::SketchObject] Sketch019
  ArcFitTolerance = 0
  AttachmentSupport = -> [XY_Plane005]
  FullyConstrained = true
  MakeInternals = false
  MapMode = 5
  sketch-geometry (5):
    g0: ArcOfCircle CenterX=0 CenterY=0 CenterZ=0 NormalX=0 NormalY=0 NormalZ=1 AngleXU=0 Radius=37 StartAngle=2.8113 EndAngle=4.39717
    g1: Circle CenterX=-15 CenterY=-46 CenterZ=0 NormalX=0 NormalY=0 NormalZ=1 AngleXU=0 Radius=8
    g2: ArcOfCircle CenterX=-15 CenterY=-46 CenterZ=0 NormalX=0 NormalY=0 NormalZ=1 AngleXU=0 Radius=11.3839 StartAngle=2.22683 EndAngle=7.53877
    g3: ArcOfCircle CenterX=0 CenterY=0 CenterZ=0 NormalX=0 NormalY=0 NormalZ=1 AngleXU=0 Radius=43 StartAngle=2.85877 EndAngle=4.17683
    g4: LineSegment StartX=-41.2916 StartY=12 StartZ=0 EndX=-35 EndY=12 EndZ=0
  constraints (14):
    c: Coincident(g0,g-1)
    c: Radius(g0) = 37
    c: Distance(g0,g-2) = 35
    c: Diameter(g1) = 16
    c: Distance(g1,g-2) = 15
    c: Coincident(g2,g1)
    c: Tangent(g2,g0) = 1.5708
    c: Coincident(g3,g0)
    c: Coincident(g2,g3)
    c: Radius(g3) = 43
    c: Coincident(g4,g3)
    c: Coincident(g4,g0)
    c: Horizontal(g4)
    c: Distance(g1,g-1) = 46
FEATURE [PartDesign::Pad] Pad013
  Direction = (0,0,1)
  Length = 5
  Length2 = 10
  Midplane = true
  Profile = -> Sketch019
  ReferenceAxis = -> Sketch019 [N_Axis]
  Suppressed = false
  Type = 0
FEATURE [PartDesign::Fillet] Fillet005
  Base = -> Pad013 [Edge8]
  BaseFeature = -> Pad013
  Radius = 10
  SupportTransform = false
  Suppressed = false
  UseAllEdges = false
FEATURE [PartDesign::Fillet] Fillet006
  Base = -> Fillet005 [Edge17,Edge12]
  BaseFeature = -> Fillet005
  Radius = 2
  SupportTransform = false
  Suppressed = false
  UseAllEdges = false
FEATURE [PartDesign::Chamfer] Chamfer002
  Angle = 45
  Base = -> Fillet006 [Edge24,Edge8]
  BaseFeature = -> Fillet006
  ChamferType = 0
  FlipDirection = false
  Size = 0.8
  Size2 = 1
  SupportTransform = false
  Suppressed = false
  UseAllEdges = false
FEATURE [PartDesign::Line] DatumLine001
  AttacherType = Attacher::AttachEngineLine
  AttachmentSupport = -> [Chamfer002]
  Length = 20
  MapMode = 42
  Placement = pos=(-15,-46,-1e-16) rot=(0,0,1;0rad)
  ResizeMode = 0
FEATURE [PartDesign::Pad] Pad014
  BaseFeature = -> Chamfer002
  Direction = (0,0,1)
  Length = 5
  Length2 = 10
  Midplane = true
  Profile = -> InvoluteGear002
  ReferenceAxis = -> InvoluteGear002 [N_Axis]
  Suppressed = false
  Type = 0
FEATURE [Sketcher::SketchObject] Sketch020
  ArcFitTolerance = 0
  AttachmentSupport = -> [Pad014]
  FullyConstrained = false
  MakeInternals = false
  MapMode = 5
  Placement = pos=(0,0,2.5) rot=(0,0,1;0rad)
  sketch-geometry (1):
    g0: Circle CenterX=-15 CenterY=-46 CenterZ=0 NormalX=0 NormalY=0 NormalZ=1 AngleXU=0 Radius=8
  constraints (1):
    c: Diameter(g0) = 16
FEATURE [PartDesign::Pocket] Pocket007
  BaseFeature = -> Pad014
  Direction = (0,0,-1)
  Length = 5
  Length2 = 5
  Profile = -> Sketch020
  ReferenceAxis = -> Sketch020 [N_Axis]
  Suppressed = false
  Type = 1
FEATURE [Sketcher::SketchObject] Sketch021
  ArcFitTolerance = 0
  AttachmentSupport = -> [Pocket007]
  ExternalGeometry = -> [Pocket007]
  FullyConstrained = true
  MakeInternals = false
  MapMode = 5
  Placement = pos=(0,0,2.5) rot=(0,0,1;0rad)
  sketch-geometry (4):
    g0: ArcOfCircle CenterX=-15 CenterY=-46 CenterZ=0 NormalX=0 NormalY=0 NormalZ=1 AngleXU=0 Radius=11.4 StartAngle=0.488692 EndAngle=1.25558
    g1: ArcOfCircle CenterX=0 CenterY=0 CenterZ=0 NormalX=0 NormalY=0 NormalZ=1 AngleXU=0 Radius=36.9839 StartAngle=4.1662 EndAngle=4.39717
    g2: ArcOfCircle CenterX=-15 CenterY=-46 CenterZ=0 NormalX=0 NormalY=0 NormalZ=1 AngleXU=0 Radius=15 StartAngle=0.488692 EndAngle=1.85533
    g3: LineSegment StartX=-4.9344 StartY=-40.648 StartZ=0 EndX=-1.75579 EndY=-38.9579 EndZ=0
  constraints (11):
    c: Coincident(g1,g-1)
    c: Coincident(g2,g0)
    c: Coincident(g2,g1)
    c: Coincident(g3,g0)
    c: Coincident(g3,g2)
    c: Radius(g0) = 11.4
    c: Tangent(g1,g0) = 1.5708
    c: Coincident(g0,g-3)
    c: Radius(g2) = 15
    c: Perpendicular(g0,g3)
    c: Angle(g-1,g3) = 0.488692
FEATURE [PartDesign::Pocket] Pocket008
  BaseFeature = -> Pocket007
  Direction = (0,0,-1)
  Length = 5
  Length2 = 5
  Profile = -> Sketch021
  ReferenceAxis = -> Sketch021 [N_Axis]
  Suppressed = false
  Type = 0
FEATURE [PartDesign::CoordinateSystem] LCS_007
  AttacherType = Attacher::AttachEngine3D
  AttachmentSupport = -> [Pocket008]
  MapMode = 11
  Placement = pos=(-15,-46,2.5) rot=(0,0,1;1.5708rad)
FEATURE [PartDesign::Body] Body004  label="bras_L"
  AllowCompound = false
  Group = -> [Sketch019,Pad013,Fillet005,Fillet006,Chamfer002,DatumLine001,InvoluteGear002,Pad014,Sketch020,Pocket007,Sketch021,Pocket008,LCS_007]
  Origin = -> Origin005
  Placement = pos=(15,46,0) rot=(0,0,1;0rad)
  Tip = -> Pocket008
FEATURE [Sketcher::SketchObject] Sketch022
  ArcFitTolerance = 0
  AttachmentSupport = -> [XY_Plane006]
  FullyConstrained = true
  MakeInternals = false
  MapMode = 5
  sketch-geometry (8):
    g0: ArcOfCircle CenterX=0 CenterY=0 CenterZ=0 NormalX=0 NormalY=0 NormalZ=1 AngleXU=0 Radius=37 StartAngle=4.41351 EndAngle=5.01126
    g1: ArcOfCircle CenterX=-13.25 CenterY=-43.0051 CenterZ=0 NormalX=0 NormalY=0 NormalZ=1 AngleXU=0 Radius=8 StartAngle=1.27192 EndAngle=4.71239
    g2: ArcOfCircle CenterX=13.25 CenterY=-43.0051 CenterZ=0 NormalX=0 NormalY=0 NormalZ=1 AngleXU=0 Radius=8 StartAngle=4.71239 EndAngle=8.15286
    g3: LineSegment StartX=-13.25 StartY=-51.0051 StartZ=0 EndX=-5 EndY=-51.0051 EndZ=0
    g4: LineSegment StartX=13.25 StartY=-51.0051 StartZ=0 EndX=5 EndY=-51.0051 EndZ=0
    g5: LineSegment StartX=-5 StartY=-51.0051 StartZ=0 EndX=-5 EndY=-86.0051 EndZ=0
    g6: LineSegment StartX=5 StartY=-51.0051 StartZ=0 EndX=5 EndY=-86.0051 EndZ=0
    g7: LineSegment StartX=-5 StartY=-86.0051 StartZ=0 EndX=5 EndY=-86.0051 EndZ=0
  constraints (24):
    c: Coincident(g0,g-1)
    c: Radius(g0) = 37
    c: Horizontal(g0,g0)
    c: Radius(g1) = 8
    c: Tangent(g1,g0) = 1.5708
    c: Radius(g2) = 8
    c: Distance(g1,g2) = 26.5
    c: Vertical(g1,g1)
    c: Vertical(g2,g2)
    c: Tangent(g2,g0) = 1.5708
    c: Coincident(g3,g1)
    c: Horizontal(g3)
    c: Coincident(g4,g2)
    c: Horizontal(g4)
    c: Equal(g3,g4)
    c: Distance(g3,g4) = 10
    c: Coincident(g5,g3)
    c: Vertical(g5)
    c: Distance(g5) = 35
    c: Coincident(g6,g4)
    c: Vertical(g6)
    c: Equal(g5,g6)
    c: Coincident(g7,g5)
    c: Coincident(g7,g6)
FEATURE [PartDesign::Pad] Pad015
  Direction = (0,0,1)
  Length = 4
  Length2 = 10
  Profile = -> Sketch022
  ReferenceAxis = -> Sketch022 [N_Axis]
  Suppressed = false
  Type = 0
FEATURE [Sketcher::SketchObject] Sketch023
  ArcFitTolerance = 0
  AttachmentSupport = -> [Pad015]
  ExternalGeometry = -> [Pad015]
  FullyConstrained = true
  MakeInternals = false
  MapMode = 5
  Placement = pos=(0,0,4) rot=(0,0,1;0rad)
  sketch-geometry (2):
    g0: Circle CenterX=-13.25 CenterY=-43.0051 CenterZ=0 NormalX=0 NormalY=0 NormalZ=1 AngleXU=0 Radius=2.6
    g1: Circle CenterX=13.25 CenterY=-43.0051 CenterZ=0 NormalX=0 NormalY=0 NormalZ=1 AngleXU=0 Radius=2.6
  constraints (4):
    c: Coincident(g0,g-3)
    c: Diameter(g0) = 5.2
    c: Coincident(g1,g-4)
    c: Equal(g1,g0)
FEATURE [PartDesign::Pad] Pad016
  BaseFeature = -> Pad015
  Direction = (0,0,1)
  Length = 5
  Length2 = 10
  Profile = -> Sketch023
  ReferenceAxis = -> Sketch023 [N_Axis]
  Suppressed = false
  Type = 0
FEATURE [Sketcher::SketchObject] Sketch024
  ArcFitTolerance = 0
  AttachmentSupport = -> [Pad016]
  ExternalGeometry = -> [Pad016]
  FullyConstrained = true
  MakeInternals = false
  MapMode = 5
  Placement = pos=(0,0,4) rot=(0,0,1;0rad)
  sketch-geometry (2):
    g0: Circle CenterX=0 CenterY=-43.5051 CenterZ=0 NormalX=0 NormalY=0 NormalZ=1 AngleXU=0 Radius=2.15
    g1: Circle CenterX=0 CenterY=-78.5051 CenterZ=0 NormalX=0 NormalY=0 NormalZ=1 AngleXU=0 Radius=2.15
  constraints (6):
    c: PointOnObject(g0,g-2)
    c: Diameter(g0) = 4.3
    c: PointOnObject(g1,g-2)
    c: Equal(g0,g1)
    c: Distance(g0,g1) = 35
    c: Distance(g0,g-3) = 7.5
FEATURE [PartDesign::Pocket] Pocket009
  BaseFeature = -> Pad016
  Direction = (0,0,-1)
  Length = 5
  Length2 = 5
  Profile = -> Sketch024
  ReferenceAxis = -> Sketch024 [N_Axis]
  Suppressed = false
  Type = 1
FEATURE [Sketcher::SketchObject] Sketch025
  ArcFitTolerance = 0
  AttachmentSupport = -> [Pocket009]
  ExternalGeometry = -> [Pocket009]
  FullyConstrained = true
  MakeInternals = false
  MapMode = 5
  Placement = pos=(0,0,4) rot=(0,0,1;0rad)
  sketch-geometry (10):
    g0: LineSegment StartX=-3.15 StartY=-46.6551 StartZ=0 EndX=-3.15 EndY=-40.3551 EndZ=0
    g1: LineSegment StartX=-3.15 StartY=-40.3551 StartZ=0 EndX=3.15 EndY=-40.3551 EndZ=0
    g2: LineSegment StartX=3.15 StartY=-40.3551 StartZ=0 EndX=3.15 EndY=-46.6551 EndZ=0
    g3: LineSegment StartX=3.15 StartY=-46.6551 StartZ=0 EndX=-3.15 EndY=-46.6551 EndZ=0
    g4: GeomPoint [constr] X=0 Y=-43.5051 Z=0
    g5: LineSegment StartX=-3.15 StartY=-81.6551 StartZ=0 EndX=-3.15 EndY=-75.3551 EndZ=0
    g6: LineSegment StartX=-3.15 StartY=-75.3551 StartZ=0 EndX=3.15 EndY=-75.3551 EndZ=0
    g7: LineSegment StartX=3.15 StartY=-75.3551 StartZ=0 EndX=3.15 EndY=-81.6551 EndZ=0
    g8: LineSegment StartX=3.15 StartY=-81.6551 StartZ=0 EndX=-3.15 EndY=-81.6551 EndZ=0
    g9: GeomPoint [constr] X=0 Y=-78.5051 Z=0
  constraints (24):
    c: Coincident(g0,g1)
    c: Coincident(g1,g2)
    c: Coincident(g2,g3)
    c: Coincident(g3,g0)
    c: Horizontal(g1)
    c: Horizontal(g3)
    c: Vertical(g0)
    c: Vertical(g2)
    c: Symmetric(g1,g0,g4)
    c: Coincident(g4,g-3)
    c: Distance(g1) = 6.3
    c: Equal(g1,g2)
    c: Coincident(g5,g6)
    c: Coincident(g6,g7)
    c: Coincident(g7,g8)
    c: Coincident(g8,g5)
    c: Horizontal(g6)
    c: Horizontal(g8)
    c: Vertical(g5)
    c: Vertical(g7)
    c: Symmetric(g6,g5,g9)
    c: Coincident(g9,g-4)
    c: Equal(g3,g6)
    c: Equal(g6,g7)
FEATURE [PartDesign::Pocket] Pocket010
  BaseFeature = -> Pocket009
  Direction = (0,0,-1)
  Length = 2.5
  Length2 = 5
  Profile = -> Sketch025
  ReferenceAxis = -> Sketch025 [N_Axis]
  Suppressed = false
  Type = 0
FEATURE [PartDesign::Fillet] Fillet007
  Base = -> Pocket010 [Edge34,Edge33,Edge35,Edge36]
  BaseFeature = -> Pocket010
  Radius = 4
  SupportTransform = false
  Suppressed = false
  UseAllEdges = false
FEATURE [PartDesign::Chamfer] Chamfer003
  Angle = 45
  Base = -> Fillet007 [Edge66,Edge72]
  BaseFeature = -> Fillet007
  ChamferType = 0
  FlipDirection = false
  Size = 1
  Size2 = 1
  SupportTransform = false
  Suppressed = false
  UseAllEdges = false
FEATURE [Sketcher::SketchObject] Sketch026
  ArcFitTolerance = 0
  AttachmentSupport = -> [Chamfer003]
  ExternalGeometry = -> [Chamfer003]
  FullyConstrained = true
  MakeInternals = false
  MapMode = 5
  Placement = pos=(0,0,4) rot=(0,0,1;0rad)
  sketch-geometry (1):
    g0: Circle CenterX=-7 CenterY=-61.0051 CenterZ=0 NormalX=0 NormalY=0 NormalZ=1 AngleXU=0 Radius=4.65
  constraints (3):
    c: Diameter(g0) = 9.3
    c: Distance(g0,g-3) = 2
    c: DistanceY(g0,g-4) = 17.5
FEATURE [PartDesign::Pocket] Pocket011
  BaseFeature = -> Chamfer003
  Direction = (0,0,-1)
  Length = 5
  Length2 = 5
  Profile = -> Sketch026
  ReferenceAxis = -> Sketch026 [N_Axis]
  Suppressed = false
  Type = 1
FEATURE [PartDesign::Fillet] Fillet008
  Base = -> Pocket011 [Edge55,Edge52]
  BaseFeature = -> Pocket011
  Radius = 3
  SupportTransform = false
  Suppressed = false
  UseAllEdges = false
FEATURE [PartDesign::CoordinateSystem] LCS_008
  AttacherType = Attacher::AttachEngine3D
  AttachmentSupport = -> [Fillet008]
  MapMode = 11
  Placement = pos=(0,-43.5051,1.5) rot=(0,0,1;1.5708rad)
FEATURE [PartDesign::CoordinateSystem] LCS_009
  AttacherType = Attacher::AttachEngine3D
  AttachmentSupport = -> [Fillet008]
  MapMode = 11
  Placement = pos=(0,-78.5051,1.5) rot=(0,0,1;1.5708rad)
FEATURE [PartDesign::CoordinateSystem] LCS_010
  AttacherType = Attacher::AttachEngine3D
  AttachmentSupport = -> [Fillet008]
  MapMode = 11
  Placement = pos=(13.25,-43.0051,8) rot=(0,0,1;1.5708rad)
FEATURE [PartDesign::CoordinateSystem] LCS_011
  AttacherType = Attacher::AttachEngine3D
  AttachmentSupport = -> [Fillet008]
  MapMode = 11
  Placement = pos=(-13.25,-43.0051,8) rot=(0,0,1;1.5708rad)
FEATURE [PartDesign::Body] Body005  label="partie_fixe_V002"
  AllowCompound = false
  Group = -> [Sketch022,Pad015,Sketch023,Pad016,Sketch024,Pocket009,Sketch025,Pocket010,Fillet007,Chamfer003,Sketch026,Pocket011,Fillet008,LCS_008,LCS_009,LCS_010,LCS_011]
  Origin = -> Origin006
  Tip = -> Fillet008
FEATURE [App::Part] Part001  label="bras_L_c"
  Group = -> [Body004]
  Origin = -> Origin007
  Placement = pos=(13,-43,6.5) rot=(0,1,0;3.14159rad)
FEATURE [App::Part] Part002  label="bras_R_c"
  Group = -> [Body001]
  Origin = -> Origin008
  Placement = pos=(-13,-43,6.5) rot=(0,0,1;0rad)
FEATURE [App::Part] Part003  label="Canapince_28BYJ"
  Group = -> [Body,Body002,Part,Body005,Part001,Part002]
  Origin = -> Origin009
FEATURE [Part::Feature] Part__Feature  label="Lever 25T"
  Placement = pos=(0,0,0) rot=(-1,0,0;1.5708rad)
  shape: bbox 18.84 x 33.03 x 6.019 mm, 125 faces (baked)
FEATURE [Part::Feature] Part__Feature001  label="Axis Servo"
  Placement = pos=(0,0,0) rot=(-1,0,0;1.5708rad)
  shape: bbox 5 x 5 x 8 mm, 5 faces (baked)
FEATURE [Part::Feature] Part__Feature002  label="Servo DS3218MG"
  Placement = pos=(0,0,0) rot=(-1,0,0;1.5708rad)
  shape: bbox 55 x 20 x 41 mm, 772 faces (baked)
FEATURE [Part::FeaturePython] Screw002  label="M2x5-Vis"  # WARN: FeaturePython — macro-defined, semantics opaque (R4)
  BaseObject = -> Body006 [Edge6]
  Diameter = 2
  Invert = true
  LeftHanded = false
  Length = 10
  LengthCustom = 5
  MatchOuter = false
  OffsetAngle = 0
  Placement = pos=(0,1e-15,4.8) rot=(0,0,1;0rad)
  Thread = false
  Type = 77
FEATURE [Sketcher::SketchObject] Sketch027
  ArcFitTolerance = 0
  AttachmentSupport = -> [XZ_Plane012]
  FullyConstrained = true
  MakeInternals = false
  MapMode = 5
  Placement = pos=(0,0,0) rot=(1,0,0;1.5708rad)
  expr: Constraints[19] = 19.8 / 2
  sketch-geometry (8):
    g0: LineSegment StartX=2.5 StartY=3.4 StartZ=0 EndX=2.5 EndY=0 EndZ=0
    g1: LineSegment StartX=2.5 StartY=0 StartZ=0 EndX=4.2 EndY=0 EndZ=0
    g2: LineSegment StartX=4.2 StartY=0 StartZ=0 EndX=4.2 EndY=2 EndZ=0
    g3: LineSegment StartX=4.2 StartY=2 StartZ=0 EndX=9.9 EndY=2 EndZ=0
    g4: LineSegment StartX=9.9 StartY=2 StartZ=0 EndX=9.9 EndY=4.4 EndZ=0
    g5: LineSegment StartX=9.9 StartY=4.4 StartZ=0 EndX=1.5 EndY=4.4 EndZ=0
    g6: LineSegment StartX=1.5 StartY=4.4 StartZ=0 EndX=1.5 EndY=3.4 EndZ=0
    g7: LineSegment StartX=1.5 StartY=3.4 StartZ=0 EndX=2.5 EndY=3.4 EndZ=0
  constraints (24):
    c: PointOnObject(g0,g-1)
    c: Vertical(g0)
    c: Coincident(g1,g0)
    c: PointOnObject(g1,g-1)
    c: Coincident(g2,g1)
    c: Vertical(g2)
    c: Coincident(g3,g2)
    c: Horizontal(g3)
    c: Coincident(g4,g3)
    c: Vertical(g4)
    c: Coincident(g5,g4)
    c: Horizontal(g5)
    c: Coincident(g6,g5)
    c: Coincident(g7,g6)
    c: Coincident(g7,g0)
    c: Horizontal(g7)
    c: Vertical(g6)
    c: DistanceY(g4,g4) = 2.4
    c: DistanceY(g2,g2) = 2
    c: DistanceX(g-1,g4) = 9.9
    c: DistanceX(g-1,g6) = 1.5
    c: DistanceY(g0,g0) = 3.4
    c: DistanceX(g-1,g0) = 2.5
    c: DistanceX(g1,g1) = 1.7
FEATURE [PartDesign::Revolution] Revolution
  Angle = 360
  Angle2 = 60
  Axis = (0,2e-16,1)
  Base = (0,0,0)
  Placement = pos=(0,0,0) rot=(1,0,0;1.5708rad)
  Profile = -> Sketch027
  ReferenceAxis = -> Sketch027 [V_Axis]
  Reversed = true
  Suppressed = false
  Type = 0
FEATURE [Sketcher::SketchObject] Sketch028
  ArcFitTolerance = 0
  AttachmentSupport = -> [XY_Plane012]
  FullyConstrained = true
  MakeInternals = false
  MapMode = 5
  sketch-geometry (1):
    g0: Circle CenterX=-7 CenterY=0 CenterZ=0 NormalX=0 NormalY=0 NormalZ=1 AngleXU=0 Radius=1.2
  constraints (3):
    c: PointOnObject(g0,g-1)
    c: Diameter(g0) = 2.4
    c: DistanceX(g0,g-1) = 7
FEATURE [PartDesign::Pocket] Pocket012
  BaseFeature = -> Revolution
  Direction = (0,0,-1)
  Length = 5
  Length2 = 5
  Midplane = true
  Placement = pos=(0,0,0) rot=(1,0,0;1.5708rad)
  Profile = -> Sketch028
  ReferenceAxis = -> Sketch028 [N_Axis]
  Suppressed = false
  Type = 1
FEATURE [PartDesign::PolarPattern] PolarPattern
  Angle = 360
  Axis = -> Sketch028 [N_Axis]
  BaseFeature = -> Pocket012
  Mode = 0
  Occurrences = 4
  Offset = 120
  Originals = -> [Pocket012]
  Placement = pos=(0,0,0) rot=(1,0,0;1.5708rad)
  Suppressed = false
  TransformMode = 0
FEATURE [PartDesign::Body] Body006  label="Corps"
  AllowCompound = false
  Group = -> [Sketch027,Revolution,Sketch028,Pocket012,PolarPattern]
  Origin = -> Origin012
  Placement = pos=(0,0,0.4) rot=(0,0,1;0rad)
  Tip = -> PolarPattern
FEATURE [App::Part] Part005  label="servo_DS3218MG"
  Group = -> [Part__Feature,Part__Feature001,Part__Feature002,Body006,Screw002]
  Origin = -> Origin011
  Placement = pos=(13,-50,0.6) rot=(0,0,1;0rad)
FEATURE [Part::Part2DObjectPython] InvoluteGear003  # Draft 2D object (typed FeaturePython)
  AddendumCoefficient = 1
  DedendumCoefficient = 1.25
  ExternalGear = true
  HighPrecision = true
  Modules = 1
  NumberOfTeeth = 26
  Placement = pos=(-13,-50,0) rot=(0,0,20;0rad)
  PressureAngle = 20
  ProfileShiftCoefficient = 0
  RootFilletCoefficient = 0.38
FEATURE [Part::Part2DObjectPython] InvoluteGear004  # Draft 2D object (typed FeaturePython)
  AddendumCoefficient = 1
  DedendumCoefficient = 1.25
  ExternalGear = true
  HighPrecision = true
  Modules = 1
  NumberOfTeeth = 26
  Placement = pos=(-13,-50,0) rot=(0,0,1;0.122173rad)
  PressureAngle = 20
  ProfileShiftCoefficient = 0
  RootFilletCoefficient = 0.38
FEATURE [Sketcher::SketchObject] Sketch029
  ArcFitTolerance = 0
  AttachmentSupport = -> [XY_Plane013]
  FullyConstrained = true
  MakeInternals = false
  MapMode = 5
  sketch-geometry (10):
    g0: ArcOfCircle CenterX=1.26e-14 CenterY=8e-14 CenterZ=0 NormalX=0 NormalY=0 NormalZ=1 AngleXU=0 Radius=37 StartAngle=2.80176 EndAngle=4.07922
    g1: Circle CenterX=-13 CenterY=-50 CenterZ=0 NormalX=0 NormalY=0 NormalZ=1 AngleXU=0 Radius=8
    g2: ArcOfCircle CenterX=-13 CenterY=-50 CenterZ=0 NormalX=0 NormalY=0 NormalZ=1 AngleXU=0 Radius=11 StartAngle=3.32671 EndAngle=7.22082
    g3: ArcOfCircle CenterX=1.26e-14 CenterY=8e-14 CenterZ=0 NormalX=0 NormalY=0 NormalZ=1 AngleXU=0 Radius=43.0969 StartAngle=2.81974 EndAngle=3.75288
    g4: LineSegment StartX=-38.9866 StartY=15 StartZ=0 EndX=-36.7696 EndY=15 EndZ=0
    g5: Circle [constr] CenterX=1.26e-14 CenterY=8e-14 CenterZ=0 NormalX=0 NormalY=0 NormalZ=1 AngleXU=0 Radius=36.5
    g6: ArcOfCircle CenterX=-92.6161 CenterY=-64.909 CenterZ=0 NormalX=0 NormalY=0 NormalZ=1 AngleXU=0 Radius=70 StartAngle=0.185117 EndAngle=0.611289
    g7: ArcOfCircle CenterX=-38.9866 CenterY=13 CenterZ=0 NormalX=0 NormalY=0 NormalZ=1 AngleXU=0 Radius=2 StartAngle=1.5708 EndAngle=2.81974
    g8: ArcOfCircle CenterX=-36.7696 CenterY=13 CenterZ=0 NormalX=0 NormalY=0 NormalZ=1 AngleXU=0 Radius=2 StartAngle=5.94335 EndAngle=7.85398
    g9: LineSegment StartX=-21.8929 StartY=-29.8278 StartZ=0 EndX=-6.49129 EndY=-41.1323 EndZ=0
  constraints (24):
    c: Coincident(g0,g-1)
    c: Radius(g0) = 37
    c: Diameter(g1) = 16
    c: Distance(g1,g-2) = 13
    c: Coincident(g2,g1)
    c: Coincident(g3,g0)
    c: Horizontal(g4)
    c: Distance(g1,g-1) = 50
    c: Coincident(g5,g0)
    c: Diameter(g5) = 73
    c: Tangent(g3,g6) = 1.5708
    c: Tangent(g4,g7) = 1.5708
    c: Tangent(g3,g7) = -1.5708
    c: Tangent(g4,g8) = 1.5708
    c: Tangent(g0,g8) = 1.5708
    c: Equal(g8,g7)
    c: Radius(g7) = 2
    c: DistanceY(g-1,g4) = 15
    c: DistanceX(g3,g0) = 6
    c: Tangent(g9,g0) = -1.5708
    c: Tangent(g9,g2) = 1.5708
    c: Tangent(g2,g6) = 1.5708
    c: Radius(g2) = 11
    c: Radius(g6) = 70
FEATURE [PartDesign::Pad] Pad017
  Direction = (0,0,1)
  Length = 5
  Length2 = 10
  Midplane = true
  Profile = -> Sketch029
  ReferenceAxis = -> Sketch029 [N_Axis]
  Suppressed = false
  Type = 0
FEATURE [PartDesign::Pad] Pad018
  BaseFeature = -> Pad017
  Direction = (0,0,1)
  Length = 5
  Length2 = 10
  Midplane = true
  Profile = -> InvoluteGear003
  ReferenceAxis = -> InvoluteGear003 [N_Axis]
  Suppressed = false
  Type = 0
FEATURE [Sketcher::SketchObject] Sketch030
  ArcFitTolerance = 0
  AttachmentSupport = -> [Pad018]
  FullyConstrained = true
  MakeInternals = false
  MapMode = 5
  Placement = pos=(0,0,2.5) rot=(0,0,1;0rad)
  sketch-geometry (2):
    g0: Circle [constr] CenterX=-13 CenterY=-50 CenterZ=0 NormalX=0 NormalY=0 NormalZ=1 AngleXU=0 Radius=8
    g1: Circle CenterX=-13 CenterY=-50 CenterZ=0 NormalX=0 NormalY=0 NormalZ=1 AngleXU=0 Radius=5
  constraints (5):
    c: Diameter(g0) = 16
    c: DistanceY(g0,g-1) = 50
    c: DistanceX(g0,g-1) = 13
    c: Diameter(g1) = 10
    c: Coincident(g1,g0)
FEATURE [Sketcher::SketchObject] Sketch032
  ArcFitTolerance = 0
  AttachmentSupport = -> [XY_Plane014]
  FullyConstrained = true
  MakeInternals = false
  MapMode = 5
  sketch-geometry (15):
    g0: ArcOfCircle CenterX=0 CenterY=0 CenterZ=0 NormalX=0 NormalY=0 NormalZ=1 AngleXU=0 Radius=37 StartAngle=2.48504 EndAngle=4.02991
    g1: ArcOfCircle CenterX=-13 CenterY=-50 CenterZ=0 NormalX=0 NormalY=0 NormalZ=1 AngleXU=0 Radius=10 StartAngle=3.01217 EndAngle=7.17151
    g2: ArcOfCircle CenterX=0 CenterY=0 CenterZ=0 NormalX=0 NormalY=0 NormalZ=1 AngleXU=0 Radius=42.891 StartAngle=2.53782 EndAngle=3.96499
    g3: LineSegment StartX=-34.073 StartY=25 StartZ=0 EndX=-30.4959 EndY=25 EndZ=0
    g4: ArcOfCircle CenterX=-42.7491 CenterY=-46.128 CenterZ=0 NormalX=0 NormalY=0 NormalZ=1 AngleXU=0 Radius=20 StartAngle=6.15376 EndAngle=7.10658
    g5: ArcOfCircle CenterX=-34.073 CenterY=23.5 CenterZ=0 NormalX=0 NormalY=0 NormalZ=1 AngleXU=0 Radius=1.5 StartAngle=1.5708 EndAngle=2.53782
    g6: ArcOfCircle CenterX=-30.4959 CenterY=23.5 CenterZ=0 NormalX=0 NormalY=0 NormalZ=1 AngleXU=0 Radius=1.5 StartAngle=5.62663 EndAngle=7.85398
    g7: Circle CenterX=-13 CenterY=-57 CenterZ=0 NormalX=0 NormalY=0 NormalZ=1 AngleXU=0 Radius=1.6
    g8: Circle CenterX=-6 CenterY=-50 CenterZ=0 NormalX=0 NormalY=0 NormalZ=1 AngleXU=0 Radius=1.6
    g9: Circle CenterX=-13 CenterY=-43 CenterZ=0 NormalX=0 NormalY=0 NormalZ=1 AngleXU=0 Radius=1.6
    g10: Circle CenterX=-20 CenterY=-50 CenterZ=0 NormalX=0 NormalY=0 NormalZ=1 AngleXU=0 Radius=1.6
    g11: LineSegment [constr] StartX=-13 StartY=-57 StartZ=0 EndX=-13 EndY=-43 EndZ=0
    g12: LineSegment [constr] StartX=-20 StartY=-50 StartZ=0 EndX=-6 EndY=-50 EndZ=0
    g13: Circle CenterX=-13 CenterY=-50 CenterZ=0 NormalX=0 NormalY=0 NormalZ=1 AngleXU=0 Radius=2.25
    g14: LineSegment StartX=-23.3365 StartY=-28.7125 StartZ=0 EndX=-6.69284 EndY=-42.2399 EndZ=0
  constraints (36):
    c: Coincident(g0,g-1)
    c: Radius(g0) = 37
    c: Coincident(g2,g0)
    c: Horizontal(g3)
    c: DistanceY(g1,g-1) = 50
    c: DistanceX(g1,g-1) = 13
    c: Tangent(g2,g4) = 1.5708
    c: Tangent(g1,g4) = 1.5708
    c: Radius(g4) = 20
    c: Tangent(g3,g5) = 1.5708
    c: Tangent(g2,g5) = -1.5708
    c: Tangent(g0,g6) = 1.5708
    c: Tangent(g3,g6) = 1.5708
    c: Equal(g6,g5)
    c: Radius(g6) = 1.5
    c: DistanceY(g-1,g3) = 25
    c: Coincident(g11,g7)
    c: Coincident(g11,g9)
    c: Vertical(g11)
    c: Coincident(g12,g10)
    c: Coincident(g12,g8)
    c: Horizontal(g12)
    c: Equal(g12,g11)
    c: Equal(g7,g10)
    c: Equal(g10,g9)
    c: Equal(g9,g8)
    c: Symmetric(g7,g9,g1)
    c: Symmetric(g8,g10,g1)
    c: DistanceY(g11,g11) = 14
    c: Diameter(g7) = 3.2
    c: Diameter(g13) = 4.5
    c: Coincident(g13,g1)
    c: DistanceX(g2,g0) = 6
    c: Radius(g1) = 10
    c: Tangent(g14,g1) = 1.5708
    c: Tangent(g14,g0) = -1.5708
FEATURE [Sketcher::SketchObject] Sketch035
  ArcFitTolerance = 0
  AttachmentSupport = -> [XY_Plane015]
  FullyConstrained = true
  MakeInternals = false
  MapMode = 5
  sketch-geometry (22):
    g0: Circle CenterX=13 CenterY=2e-16 CenterZ=0 NormalX=0 NormalY=0 NormalZ=1 AngleXU=0 Radius=7
    g1: LineSegment StartX=-23.5 StartY=10 StartZ=0 EndX=-23.5 EndY=-10 EndZ=0
    g2: LineSegment StartX=-21.5 StartY=-12 StartZ=0 EndX=28.5 EndY=-12 EndZ=0
    g3: LineSegment StartX=30.5 StartY=-10 StartZ=0 EndX=30.5 EndY=10 EndZ=0
    g4: ArcOfCircle CenterX=-21.5 CenterY=10 CenterZ=0 NormalX=0 NormalY=0 NormalZ=1 AngleXU=0 Radius=2 StartAngle=1.5708 EndAngle=3.14159
    g5: ArcOfCircle CenterX=-21.5 CenterY=-10 CenterZ=0 NormalX=0 NormalY=0 NormalZ=1 AngleXU=0 Radius=2 StartAngle=3.14159 EndAngle=4.71239
    g6: ArcOfCircle CenterX=28.5 CenterY=-10 CenterZ=0 NormalX=0 NormalY=0 NormalZ=1 AngleXU=0 Radius=2 StartAngle=4.71239 EndAngle=6.28319
    g7: GeomPoint [constr] X=30.5 Y=-12 Z=0
    g8: LineSegment [constr] StartX=-21.5 StartY=6 StartZ=0 EndX=-21.5 EndY=-6 EndZ=0
    g9: LineSegment [constr] StartX=-21.5 StartY=-6 StartZ=0 EndX=28.5 EndY=-6 EndZ=0
    g10: LineSegment [constr] StartX=28.5 StartY=-6 StartZ=0 EndX=28.5 EndY=6 EndZ=0
    g11: LineSegment [constr] StartX=28.5 StartY=6 StartZ=0 EndX=-21.5 EndY=6 EndZ=0
    g12: LineSegment [constr] StartX=-21.5 StartY=-3e-16 StartZ=0 EndX=28.5 EndY=4e-16 EndZ=0
    g13: Circle CenterX=-21.5 CenterY=6 CenterZ=0 NormalX=0 NormalY=0 NormalZ=1 AngleXU=0 Radius=1.85
    g14: Circle CenterX=-21.5 CenterY=-6 CenterZ=0 NormalX=0 NormalY=0 NormalZ=1 AngleXU=0 Radius=1.85
    g15: Circle CenterX=28.5 CenterY=6 CenterZ=0 NormalX=0 NormalY=0 NormalZ=1 AngleXU=0 Radius=1.85
    g16: Circle CenterX=28.5 CenterY=-6 CenterZ=0 NormalX=0 NormalY=0 NormalZ=1 AngleXU=0 Radius=1.85
    g17: Circle CenterX=-13 CenterY=-2e-16 CenterZ=0 NormalX=0 NormalY=0 NormalZ=1 AngleXU=0 Radius=1.85
    g18: LineSegment StartX=-21.5 StartY=12 StartZ=0 EndX=-8 EndY=12 EndZ=0
    g19: ArcOfCircle CenterX=28.5 CenterY=10 CenterZ=0 NormalX=0 NormalY=0 NormalZ=1 AngleXU=0 Radius=2 StartAngle=1e-16 EndAngle=1.5708
    g20: LineSegment StartX=8 StartY=12 StartZ=0 EndX=28.5 EndY=12 EndZ=0
    g21: ArcOfCircle CenterX=7.5e-15 CenterY=50 CenterZ=0 NormalX=0 NormalY=0 NormalZ=1 AngleXU=0 Radius=38.833 StartAngle=4.50489 EndAngle=4.91989
  constraints (56):
    c: Diameter(g0) = 14
    c: Tangent(g1,g4) = -1.5708
    c: Tangent(g1,g5) = -1.5708
    c: Tangent(g2,g5) = -1.5708
    c: Tangent(g2,g6) = -1.5708
    c: Tangent(g3,g6) = -1.5708
    c: Vertical(g1)
    c: Vertical(g3)
    c: Horizontal(g2)
    c: Equal(g4,g5)
    c: Equal(g5,g6)
    c: PointOnObject(g7,g2)
    c: PointOnObject(g7,g3)
    c: Coincident(g8,g9)
    c: Coincident(g9,g10)
    c: Coincident(g10,g11)
    c: Coincident(g11,g8)
    c: Vertical(g10)
    c: DistanceX(g11,g11) = 50
    c: DistanceY(g8,g8) = 12
    c: Symmetric(g8,g8,g12)
    c: Symmetric(g10,g10,g12)
    c: PointOnObject(g0,g12)
    c: Diameter(g13) = 3.7
    c: Equal(g16,g15)
    c: Equal(g15,g14)
    c: Equal(g14,g13)
    c: PointOnObject(g-1,g12)
    c: PointOnObject(g17,g12)
    c: DistanceX(g17,g-1) = 13
    c: Equal(g17,g13)
    c: DistanceY(g2,g5) = 2
    c: Tangent(g3,g19) = -1.5708
    c: Coincident(g10,g15)
    c: DistanceX(g5,g-1) = 21.5
    c: Equal(g19,g4)
    c: Coincident(g8,g13)
    c: Vertical(g8)
    c: Tangent(g18,g4) = 1.5708
    c: Horizontal(g18)
    c: Horizontal(g11)
    c: DistanceX(g-1,g0) = 13
    c: Coincident(g9,g16)
    c: Horizontal(g9)
    c: Coincident(g8,g14)
    c: DistanceX(g12,g-1) = 21.5
    c: Vertical(g9,g6)
    c: DistanceY(g6,g9) = 4
    c: DistanceY(g10,g19) = 4
    c: Tangent(g20,g19) = 1.5708
    c: Symmetric(g18,g20,g-2)
    c: Horizontal(g20)
    c: Coincident(g21,g18)
    c: Coincident(g21,g20)
    c: DistanceY(g-1,g21) = 50
    c: DistanceX(g-1,g20) = 8
FEATURE [PartDesign::Pad] Pad021
  Direction = (0,0,1)
  Length = 5.4
  Length2 = 10.3
  Profile = -> Sketch035
  ReferenceAxis = -> Sketch035 [N_Axis]
  Suppressed = false
  Type = 4
FEATURE [PartDesign::Pad] Pad023
  Direction = (0,0,1)
  Length = 5
  Length2 = 10
  Midplane = true
  Placement = pos=(-13,-50,0) rot=(0,0,1;0.122173rad)
  Profile = -> InvoluteGear004
  ReferenceAxis = -> InvoluteGear004 [N_Axis]
  Suppressed = false
  Type = 0
FEATURE [PartDesign::Pad] Pad024
  BaseFeature = -> Pad023
  Direction = (0,0,1)
  Length = 5
  Length2 = 10
  Midplane = true
  Placement = pos=(-13,-50,0) rot=(0,0,1;0.122173rad)
  Profile = -> Sketch032
  ReferenceAxis = -> Sketch032 [N_Axis]
  Suppressed = false
  Type = 0
FEATURE [Mesh::Feature] open_tin_can001
  Placement = pos=(0,0,-97) rot=(-1,0,0;1.5708rad)
FEATURE [Sketcher::SketchObject] Sketch038
  ArcFitTolerance = 1e-06
  AttachmentSupport = -> [XZ_Plane015]
  ExternalGeometry = -> [Pad021]
  FullyConstrained = true
  MakeInternals = false
  MapMode = 5
  Placement = pos=(0,0,0) rot=(1,0,0;1.5708rad)
  sketch-geometry (9):
    g0: LineSegment StartX=-16.5 StartY=-3 StartZ=0 EndX=-16.5 EndY=-20 EndZ=0
    g1: LineSegment StartX=-16.5 StartY=-20 StartZ=0 EndX=23.5 EndY=-20 EndZ=0
    g2: LineSegment StartX=23.5 StartY=-20 StartZ=0 EndX=23.5 EndY=-3 EndZ=0
    g3: LineSegment StartX=20.5 StartY=0 StartZ=0 EndX=-13.5 EndY=0 EndZ=0
    g4: LineSegment [constr] StartX=3.5 StartY=0 StartZ=0 EndX=3.5 EndY=-20 EndZ=0
    g5: ArcOfCircle CenterX=-13.5 CenterY=-3 CenterZ=0 NormalX=0 NormalY=0 NormalZ=1 AngleXU=0 Radius=3 StartAngle=1.5708 EndAngle=3.14159
    g6: GeomPoint [constr] X=-16.5 Y=0 Z=0
    g7: ArcOfCircle CenterX=20.5 CenterY=-3 CenterZ=0 NormalX=0 NormalY=0 NormalZ=1 AngleXU=0 Radius=3 StartAngle=1e-16 EndAngle=1.5708
    g8: GeomPoint [constr] X=23.5 Y=0 Z=0
  constraints (22):
    c: Coincident(g0,g1)
    c: Coincident(g1,g2)
    c: Vertical(g0)
    c: Vertical(g2)
    c: Horizontal(g1)
    c: Horizontal(g3)
    c: PointOnObject(g6,g-1)
    c: DistanceY(g0,g6) = 20
    c: DistanceX(g1,g1) = 40
    c: Symmetric(g8,g6,g4)
    c: Symmetric(g1,g1,g4)
    c: DistanceX(g-1,g4) = 3.5
    c: PointOnObject(g6,g3)
    c: PointOnObject(g6,g0)
    c: Tangent(g3,g5) = -1.5708
    c: Tangent(g0,g5) = -1.5708
    c: PointOnObject(g8,g3)
    c: PointOnObject(g8,g2)
    c: Tangent(g3,g7) = -1.5708
    c: Tangent(g2,g7) = -1.5708
    c: Equal(g7,g5)
    c: Radius(g5) = 3
FEATURE [PartDesign::Pocket] Pocket019
  BaseFeature = -> Pad021
  Direction = (0,1,-2e-16)
  Length = 20.2
  Length2 = 5
  Midplane = true
  Profile = -> Sketch038
  ReferenceAxis = -> Sketch038 [N_Axis]
  Suppressed = false
  Type = 0
FEATURE [Sketcher::SketchObject] Sketch039
  ArcFitTolerance = 1e-06
  AttachmentSupport = -> [Pocket019]
  ExternalGeometry = -> [Pocket019]
  FullyConstrained = true
  MakeInternals = false
  MapMode = 5
  Placement = pos=(-23.5,0,0) rot=(0.57735,-0.57735,-0.57735;2.0944rad)
  sketch-geometry (5):
    g0: LineSegment StartX=-0.85 StartY=0 StartZ=0 EndX=-0.85 EndY=-20 EndZ=0
    g1: LineSegment StartX=-0.85 StartY=-20 StartZ=0 EndX=0.85 EndY=-20 EndZ=0
    g2: LineSegment StartX=0.85 StartY=-20 StartZ=0 EndX=0.85 EndY=0 EndZ=0
    g3: LineSegment StartX=0.85 StartY=0 StartZ=0 EndX=-0.85 EndY=0 EndZ=0
    g4: LineSegment [constr] StartX=1e-16 StartY=5.4 StartZ=0 EndX=1e-16 EndY=0 EndZ=0
  constraints (14):
    c: Coincident(g0,g1)
    c: Coincident(g1,g2)
    c: Coincident(g2,g3)
    c: Coincident(g3,g0)
    c: Vertical(g0)
    c: Vertical(g2)
    c: Horizontal(g1)
    c: Horizontal(g3)
    c: PointOnObject(g0,g-1)
    c: Symmetric(g-3,g-3,g4)
    c: Symmetric(g3,g3,g4)
    c: Vertical(g4)
    c: DistanceY(g2,g2) = 20
    c: DistanceX(g3,g3) = 1.7
FEATURE [PartDesign::Pocket] Pocket020
  BaseFeature = -> Pocket019
  Direction = (1,0,0)
  Length = 5
  Length2 = 5
  Profile = -> Sketch039
  ReferenceAxis = -> Sketch039 [N_Axis]
  Suppressed = false
  Type = 1
FEATURE [Sketcher::SketchObject] Sketch040
  ArcFitTolerance = 1e-06
  AttachmentSupport = -> [YZ_Plane018]
  FullyConstrained = true
  MakeInternals = false
  MapMode = 5
  Placement = pos=(0,0,0) rot=(0.57735,0.57735,0.57735;2.0944rad)
  sketch-geometry (10):
    g0: LineSegment StartX=-36.5 StartY=0 StartZ=0 EndX=-36.5 EndY=108 EndZ=0
    g1: ArcOfCircle CenterX=-37.5 CenterY=108 CenterZ=0 NormalX=0 NormalY=0 NormalZ=1 AngleXU=0 Radius=1 StartAngle=3e-15 EndAngle=1.5708
    g2: LineSegment StartX=-37.5 StartY=109 StartZ=0 EndX=-38.5 EndY=109 EndZ=0
    g3: LineSegment StartX=0 StartY=0 StartZ=0 EndX=0 EndY=1 EndZ=0
    g4: LineSegment StartX=-36.5 StartY=0 StartZ=0 EndX=0 EndY=0 EndZ=0
    g5: LineSegment StartX=-38.5 StartY=109 StartZ=0 EndX=-38.5 EndY=110 EndZ=0
    g6: LineSegment StartX=-38.5 StartY=110 StartZ=0 EndX=-37.5 EndY=110 EndZ=0
    g7: LineSegment StartX=-35.5 StartY=108 StartZ=0 EndX=-35.5 EndY=1 EndZ=0
    g8: LineSegment StartX=-35.5 StartY=1 StartZ=0 EndX=0 EndY=1 EndZ=0
    g9: ArcOfCircle CenterX=-37.5 CenterY=108 CenterZ=0 NormalX=0 NormalY=0 NormalZ=1 AngleXU=0 Radius=2 StartAngle=9e-16 EndAngle=1.5708
  constraints (26):
    c: Vertical(g0)
    c: Tangent(g0,g1) = -1.5708
    c: Tangent(g1,g2) = -1.5708
    c: Horizontal(g2)
    c: DistanceY(g-1,g2) = 109
    c: Coincident(g4,g3)
    c: Vertical(g3)
    c: Horizontal(g4)
    c: Coincident(g3,g-1)
    c: Coincident(g0,g4)
    c: Distance(g5) = 1
    c: Coincident(g5,g2)
    c: Vertical(g5)
    c: Coincident(g6,g5)
    c: Horizontal(g6)
    c: Vertical(g7)
    c: Coincident(g8,g7)
    c: Coincident(g8,g3)
    c: Horizontal(g8)
    c: Equal(g3,g5)
    c: Coincident(g9,g1)
    c: Tangent(g9,g6) = 1.5708
    c: DistanceX(g5,g0) = 2
    c: Radius(g1) = 1
    c: Tangent(g9,g7) = 1.5708
    c: DistanceX(g4,g4) = 36.5
FEATURE [PartDesign::Revolution] Revolution001
  Angle = 360
  Angle2 = 60
  Axis = (0,0,1)
  Base = (0,0,0)
  Placement = pos=(0,0,0) rot=(1,1,1;2.0944rad)
  Profile = -> Sketch040
  ReferenceAxis = -> Sketch040 [V_Axis]
  Suppressed = false
  Type = 0
FEATURE [PartDesign::Body] Body010  label="canette"
  AllowCompound = false
  Group = -> [Sketch040,Revolution001]
  Origin = -> Origin018
  Placement = pos=(-9.8e-15,0,20) rot=(0,1,0;3.14159rad)
  Tip = -> Revolution001
FEATURE [Sketcher::SketchObject] Sketch042
  ArcFitTolerance = 1e-06
  AttachmentSupport = -> [XZ_Plane019]
  FullyConstrained = true
  MakeInternals = false
  MapMode = 5
  Placement = pos=(0,0,0) rot=(1,0,0;1.5708rad)
  expr: Constraints[18] = 3.5 / 2
  expr: Constraints[19] = 5.5 / 2
  expr: Constraints[4] = 9.8 / 2
  sketch-geometry (12):
    g0: LineSegment StartX=-3.75 StartY=7.4 StartZ=0 EndX=-6.75 EndY=7.4 EndZ=0
    g1: LineSegment StartX=-2.75 StartY=6.4 StartZ=0 EndX=-2.75 EndY=3 EndZ=0
    g2: LineSegment StartX=-4.9 StartY=0 StartZ=0 EndX=-1.75 EndY=0 EndZ=0
    g3: LineSegment StartX=-7.75 StartY=6.4 StartZ=0 EndX=-7.75 EndY=5 EndZ=0
    g4: LineSegment StartX=-7.75 StartY=5 StartZ=0 EndX=-4.9 EndY=5 EndZ=0
    g5: LineSegment StartX=-4.9 StartY=5 StartZ=0 EndX=-4.9 EndY=0 EndZ=0
    g6: LineSegment StartX=-2.75 StartY=3 StartZ=0 EndX=-1.75 EndY=3 EndZ=0
    g7: LineSegment StartX=-1.75 StartY=3 StartZ=0 EndX=-1.75 EndY=0 EndZ=0
    g8: ArcOfCircle CenterX=-3.75 CenterY=6.4 CenterZ=0 NormalX=0 NormalY=0 NormalZ=1 AngleXU=0 Radius=1 StartAngle=-2.7e-15 EndAngle=1.5708
    g9: GeomPoint [constr] X=-2.75 Y=7.4 Z=0
    g10: ArcOfCircle CenterX=-6.75 CenterY=6.4 CenterZ=0 NormalX=0 NormalY=0 NormalZ=1 AngleXU=0 Radius=1 StartAngle=1.5708 EndAngle=3.14159
    g11: GeomPoint [constr] X=-7.75 Y=7.4 Z=0
  constraints (33):
    c: Horizontal(g0)
    c: Vertical(g1)
    c: Coincident(g2,g5)
    c: Horizontal(g2)
    c: DistanceX(g5,g-1) = 4.9
    c: Coincident(g3,g4)
    c: Vertical(g3)
    c: Horizontal(g4)
    c: PointOnObject(g4,g5)
    c: PointOnObject(g5,g4)
    c: Vertical(g5)
    c: DistanceY(g3,g11) = 2.4
    c: PointOnObject(g2,g-1)
    c: Horizontal(g6)
    c: Coincident(g7,g6)
    c: Vertical(g7)
    c: Coincident(g1,g6)
    c: Coincident(g2,g7)
    c: DistanceX(g2,g-1) = 1.75
    c: DistanceX(g1,g-1) = 2.75
    c: DistanceY(g7,g7) = 3
    c: DistanceY(g5,g5) = 5
    c: DistanceX(g11,g9) = 5
    c: PointOnObject(g9,g0)
    c: PointOnObject(g9,g1)
    c: Tangent(g0,g8) = -1.5708
    c: Tangent(g1,g8) = 1.5708
    c: Radius(g8) = 1
    c: PointOnObject(g11,g0)
    c: PointOnObject(g11,g3)
    c: Tangent(g0,g10) = -1.5708
    c: Tangent(g3,g10) = -1.5708
    c: Equal(g10,g8)
FEATURE [PartDesign::Revolution] Revolution002
  Angle = 360
  Angle2 = 60
  Axis = (0,2e-16,1)
  Base = (0,0,0)
  Placement = pos=(0,0,0) rot=(1,0,0;1.5708rad)
  Profile = -> Sketch042
  ReferenceAxis = -> Sketch042 [V_Axis]
  Suppressed = false
  Type = 0
FEATURE [PartDesign::Body] Body011  label="Axe_bras_G"
  AllowCompound = false
  Group = -> [Sketch042,Revolution002]
  Origin = -> Origin019
  Placement = pos=(-13,-50,5.4) rot=(0,0,1;0rad)
  Tip = -> Revolution002
FEATURE [PartDesign::Pocket] Pocket013
  BaseFeature = -> Pad018
  Direction = (0,0,-1)
  Length = 5
  Length2 = 5
  Profile = -> Sketch030
  ReferenceAxis = -> Sketch030 [N_Axis]
  Suppressed = false
  Type = 1
FEATURE [PartDesign::Pocket] Pocket022
  BaseFeature = -> Pad024
  Direction = (0,0,1)
  Length = 5
  Length2 = 5
  Placement = pos=(-13,-50,0) rot=(0,0,1;0.122173rad)
  Profile = -> Pad024 [Face227,Face230,Face228,Face229,Face226]
  Suppressed = false
  Type = 1
FEATURE [Sketcher::SketchObject] Sketch043
  ArcFitTolerance = 1e-06
  AttachmentSupport = -> [Pocket020]
  ExternalGeometry = -> [Pocket020]
  FullyConstrained = true
  MakeInternals = false
  MapMode = 5
  Placement = pos=(0,0,5.4) rot=(0,0,1;0rad)
  sketch-geometry (1):
    g0: Circle CenterX=13 CenterY=0 CenterZ=0 NormalX=0 NormalY=0 NormalZ=1 AngleXU=0 Radius=10.25
  constraints (2):
    c: Diameter(g0) = 20.5
    c: Coincident(g0,g-3)
FEATURE [PartDesign::Pocket] Pocket023
  BaseFeature = -> Pocket020
  Direction = (0,0,-1)
  Length = 7
  Length2 = 5
  Profile = -> Sketch043
  ReferenceAxis = -> Sketch043 [N_Axis]
  Suppressed = false
  Type = 0
FEATURE [Sketcher::SketchObject] Sketch044
  ArcFitTolerance = 1e-06
  AttachmentOffset = pos=(0,-2.45,12) rot=(0,0,1;0rad)
  AttachmentSupport = -> [XZ_Plane015]
  ExternalGeometry = -> [Pocket023]
  FullyConstrained = true
  MakeInternals = false
  MapMode = 5
  Placement = pos=(0,-12,-2.45) rot=(1,0,0;1.5708rad)
  sketch-geometry (6):
    g0: LineSegment StartX=-10 StartY=0 StartZ=0 EndX=-10 EndY=7.85 EndZ=0
    g1: LineSegment StartX=-10 StartY=7.85 StartZ=0 EndX=-20 EndY=7.85 EndZ=0
    g2: LineSegment StartX=-20 StartY=7.85 StartZ=0 EndX=-20 EndY=0 EndZ=0
    g3: LineSegment StartX=-20 StartY=0 StartZ=0 EndX=-10 EndY=0 EndZ=0
    g4: LineSegment [constr] StartX=-20 StartY=3.925 StartZ=0 EndX=-10 EndY=3.925 EndZ=0
    g5: GeomPoint [constr] X=-15 Y=3.925 Z=0
  constraints (16):
    c: Coincident(g2,g3)
    c: Vertical(g0)
    c: Vertical(g2)
    c: Horizontal(g1)
    c: Horizontal(g3)
    c: Coincident(g0,g3)
    c: Coincident(g0,g1)
    c: PointOnObject(g0,g-1)
    c: PointOnObject(g4,g2)
    c: Horizontal(g4)
    c: Coincident(g1,g2)
    c: PointOnObject(g1,g-3)
    c: DistanceX(g1,g1) = 10
    c: Symmetric(g4,g4,g5)
    c: DistanceX(g5,g-1) = 15
    c: Symmetric(g0,g0,g4)
FEATURE [PartDesign::Pad] Pad025
  BaseFeature = -> Pocket023
  Direction = (0,-1,2e-16)
  Length = 22
  Length2 = 10
  Profile = -> Sketch044
  ReferenceAxis = -> Sketch044 [N_Axis]
  Suppressed = false
  Type = 0
FEATURE [PartDesign::Mirrored] Mirrored002
  MirrorPlane = -> Sketch044 [V_Axis]
  Suppressed = false
  TransformMode = 0
FEATURE [PartDesign::Mirrored] Mirrored003
  MirrorPlane = -> Sketch044 [H_Axis]
  Suppressed = false
  TransformMode = 0
FEATURE [Sketcher::SketchObject] Sketch045
  ArcFitTolerance = 1e-06
  AttachmentSupport = -> [Pad025]
  ExternalGeometry = -> [Pad025]
  FullyConstrained = true
  MakeInternals = false
  MapMode = 5
  Placement = pos=(0,-34,7.7e-15) rot=(1,0,0;1.5708rad)
  sketch-geometry (2):
    g0: LineSegment [constr] StartX=-20 StartY=5.4 StartZ=0 EndX=-10 EndY=-2.45 EndZ=0
    g1: Circle CenterX=-15 CenterY=1.475 CenterZ=0 NormalX=0 NormalY=0 NormalZ=1 AngleXU=0 Radius=1.85
  constraints (4):
    c: Coincident(g0,g-3)
    c: Coincident(g0,g-4)
    c: Symmetric(g0,g0,g1)
    c: Diameter(g1) = 3.7
FEATURE [PartDesign::Pocket] Pocket024
  BaseFeature = -> Pad025
  Direction = (0,1,-2e-16)
  Length = 12
  Length2 = 5
  Profile = -> Sketch045
  ReferenceAxis = -> Sketch045 [N_Axis]
  Suppressed = false
  Type = 0
FEATURE [Sketcher::SketchObject] Sketch046
  ArcFitTolerance = 1e-06
  AttachmentSupport = -> [Pocket024]
  ExternalGeometry = -> [Pocket024]
  FullyConstrained = true
  MakeInternals = false
  MapMode = 5
  Placement = pos=(0,-34,7.7e-15) rot=(1,0,0;1.5708rad)
  sketch-geometry (1):
    g0: Circle CenterX=-15 CenterY=1.475 CenterZ=0 NormalX=0 NormalY=0 NormalZ=1 AngleXU=0 Radius=2.1
  constraints (2):
    c: Diameter(g0) = 4.2
    c: Coincident(g0,g-3)
FEATURE [PartDesign::Pocket] Pocket025
  BaseFeature = -> Pocket024
  Direction = (0,1,-2e-16)
  Length = 2
  Length2 = 5
  Profile = -> Sketch046
  ReferenceAxis = -> Sketch046 [N_Axis]
  Suppressed = false
  Type = 0
FEATURE [PartDesign::MultiTransform] MultiTransform
  BaseFeature = -> Pocket025
  Originals = -> [Pad025,Pocket024,Pocket025]
  Refine = true
  Suppressed = false
  TransformMode = 0
  Transformations = -> [Mirrored002,Mirrored003]
FEATURE [PartDesign::Fillet] Fillet009
  Base = -> MultiTransform [Edge78,Edge140,Edge138,Edge4]
  BaseFeature = -> MultiTransform
  Radius = 4
  SupportTransform = false
  Suppressed = false
  UseAllEdges = false
FEATURE [PartDesign::Body] Body009  label="partie_fixe"
  AllowCompound = false
  Group = -> [Sketch035,Pad021,Sketch038,Pocket019,Sketch039,Pocket020,Sketch043,Pocket023,Sketch044,Pad025,Sketch045,Pocket024,Sketch046,Pocket025,MultiTransform,Mirrored002,Mirrored003,Fillet009]
  Origin = -> Origin015
  Placement = pos=(0,-50,0) rot=(0,0,1;0rad)
  Tip = -> Fillet009
FEATURE [App::VarSet] VarSet
  Position_pince = 60
FEATURE [Sketcher::SketchObject] Sketch047
  ArcFitTolerance = 1e-06
  AttachmentOffset = pos=(0,0,2.5) rot=(0,0,1;0rad)
  AttachmentSupport = -> [XY_Plane014]
  ExternalGeometry = -> [Pocket022]
  FullyConstrained = false
  MakeInternals = false
  MapMode = 5
  Placement = pos=(0,0,2.5) rot=(0,0,1;0rad)
  sketch-geometry (6):
    g0: ArcOfCircle CenterX=-5.3e-15 CenterY=0 CenterZ=0 NormalX=0 NormalY=0 NormalZ=1 AngleXU=0 Radius=37 StartAngle=2.48504 EndAngle=3.88745
    g1: ArcOfCircle CenterX=-5.3e-15 CenterY=0 CenterZ=0 NormalX=0 NormalY=0 NormalZ=1 AngleXU=0 Radius=42.891 StartAngle=2.53782 EndAngle=3.89288
    g2: ArcOfCircle CenterX=-34.073 CenterY=23.5 CenterZ=0 NormalX=0 NormalY=0 NormalZ=1 AngleXU=0 Radius=1.5 StartAngle=1.5708 EndAngle=2.53782
    g3: ArcOfCircle CenterX=-30.4959 CenterY=23.5 CenterZ=0 NormalX=0 NormalY=0 NormalZ=1 AngleXU=0 Radius=1.5 StartAngle=5.62663 EndAngle=7.85398
    g4: LineSegment StartX=-34.073 StartY=25 StartZ=0 EndX=-30.4959 EndY=25 EndZ=0
    g5: LineSegment StartX=-31.3452 StartY=-29.2766 StartZ=0 EndX=-27.1768 EndY=-25.1082 EndZ=0
  constraints (12):
    c: Coincident(g0,g-4)
    c: Coincident(g1,g0)
    c: Coincident(g1,g-4)
    c: Tangent(g0,g3) = 1.5708
    c: Tangent(g2,g1) = -1.5708
    c: Tangent(g4,g2) = 1.5708
    c: Tangent(g4,g3) = 1.5708
    c: Coincident(g-7,g2)
    c: Coincident(g0,g-5)
    c: Coincident(g5,g1)
    c: Coincident(g5,g0)
    c: Angle(g5,g-2) = 0.785398
FEATURE [PartDesign::Pad] Pad026
  BaseFeature = -> Pocket022
  Direction = (0,0,1)
  Length = 30
  Length2 = 10
  Placement = pos=(-13,-50,0) rot=(0,0,1;0.122173rad)
  Profile = -> Sketch047
  ReferenceAxis = -> Sketch047 [N_Axis]
  Suppressed = false
  Type = 0
FEATURE [Sketcher::SketchObject] Sketch048
  ArcFitTolerance = 1e-06
  AttachmentSupport = -> [Pocket013]
  ExternalGeometry = -> [Pocket013]
  FullyConstrained = true
  MakeInternals = false
  MapMode = 5
  Placement = pos=(0,0,-2.5) rot=(1,0,0;3.14159rad)
  sketch-geometry (6):
    g0: ArcOfCircle CenterX=-36.7696 CenterY=-13 CenterZ=0 NormalX=0 NormalY=0 NormalZ=1 AngleXU=0 Radius=2 StartAngle=4.71238 EndAngle=6.62302
    g1: ArcOfCircle CenterX=-38.9866 CenterY=-13 CenterZ=0 NormalX=0 NormalY=0 NormalZ=1 AngleXU=0 Radius=2 StartAngle=3.46345 EndAngle=4.71239
    g2: ArcOfCircle CenterX=1.26e-14 CenterY=-8e-14 CenterZ=0 NormalX=0 NormalY=0 NormalZ=1 AngleXU=0 Radius=37 StartAngle=2.37418 EndAngle=3.48143
    g3: ArcOfCircle CenterX=1.26e-14 CenterY=-8e-14 CenterZ=0 NormalX=0 NormalY=0 NormalZ=1 AngleXU=0 Radius=43.0969 StartAngle=2.37163 EndAngle=3.46345
    g4: LineSegment StartX=-30.941 StartY=30 StartZ=0 EndX=-26.6292 EndY=25.6882 EndZ=0
    g5: LineSegment StartX=-38.9866 StartY=-15 StartZ=0 EndX=-36.7696 EndY=-15 EndZ=0
  constraints (15):
    c: Coincident(g0,g-6)
    c: Coincident(g0,g-6)
    c: Coincident(g1,g-7)
    c: Coincident(g1,g-7)
    c: Coincident(g2,g0)
    c: Coincident(g3,g2)
    c: Coincident(g3,g1)
    c: Coincident(g2,g-3)
    c: Coincident(g4,g3)
    c: Coincident(g4,g2)
    c: Angle(g-2,g4) = 0.785398
    c: DistanceY(g-1,g3) = 30
    c: Coincident(g5,g0)
    c: Horizontal(g5)
    c: Tangent(g5,g1) = -1.5708
FEATURE [PartDesign::Pad] Pad027
  BaseFeature = -> Pocket013
  Direction = (0,0,-1)
  Length = 20
  Length2 = 10
  Profile = -> Sketch048
  ReferenceAxis = -> Sketch048 [N_Axis]
  Suppressed = false
  Type = 0
FEATURE [Part::FeaturePython] HoneycombSolid  # WARN: FeaturePython — macro-defined, semantics opaque (R4)
  Circumradius = 3.2
  Height = 20
  Length = 10
  Placement = pos=(-27.2176,25.4319,-5) rot=(0.129428,-0.983106,-0.129428;4.69535rad)
  Thickness = 1
  UseContainer = false
  Width = 30
FEATURE [Part::FeaturePython] HoneycombSolid001  # WARN: FeaturePython — macro-defined, semantics opaque (R4)
  Circumradius = 3.1
  Height = 20
  Length = 20
  Placement = pos=(12.1427,31.3165,-5) rot=(0,1,0;1.5708rad)
  Thickness = 1
  UseContainer = false
  Width = 34
FEATURE [PartDesign::Chamfer] Chamfer004
  Angle = 45
  Base = -> Pad026 [Edge803]
  BaseFeature = -> Pad026
  ChamferType = 0
  FlipDirection = false
  Placement = pos=(-13,-50,0) rot=(0,0,1;0.122173rad)
  Size = 6
  Size2 = 1
  SupportTransform = false
  Suppressed = false
  UseAllEdges = false
FEATURE [PartDesign::Body] Body008  label="bras_D001"
  AllowCompound = false
  Group = -> [Sketch032,InvoluteGear004,Pad023,Pad024,Pocket022,Sketch047,Pad026,Chamfer004]
  Origin = -> Origin014
  Placement = pos=(-13,50,-3.2e-15) rot=(0,1,0;3.14159rad)
  Tip = -> Chamfer004
FEATURE [Part::Cut] Cut001
  Base = -> Body008
  Tool = -> HoneycombSolid001
FEATURE [App::Part] Part006  label="bras_D"
  Group = -> [Body008,HoneycombSolid001,Cut001]
  Origin = -> Origin016
  Placement = pos=(13,-50,7.9) rot=(0,0,1;-1.0472rad)
  expr: .Placement.Rotation.Angle = -<<bras_G>>.Placement.Rotation.Angle
FEATURE [PartDesign::Chamfer] Chamfer005
  Angle = 45
  Base = -> Pad027 [Edge88]
  BaseFeature = -> Pad027
  ChamferType = 0
  FlipDirection = false
  Size = 5
  Size2 = 1
  SupportTransform = false
  Suppressed = false
  UseAllEdges = false
FEATURE [PartDesign::Body] Body007  label="bras_G001"
  AllowCompound = false
  Group = -> [Sketch029,Pad017,InvoluteGear003,Pad018,Sketch030,Pocket013,Sketch048,Pad027,Chamfer005]
  Origin = -> Origin013
  Placement = pos=(13,50,0) rot=(0,0,1;0rad)
  Tip = -> Chamfer005
FEATURE [Part::Cut] Cut
  Base = -> Body007
  Tool = -> HoneycombSolid
FEATURE [App::Part] Part007  label="bras_G"
  Group = -> [Body007,HoneycombSolid,Cut]
  Origin = -> Origin017
  Placement = pos=(-13,-50,7.9) rot=(0,0,1;1.0472rad)
  expr: .Placement.Rotation.Angle = VarSet.Position_pince
FEATURE [App::Part] Part004  label="CanaPince_Servomoteur"
  Group = -> [Part005,Body009,Body011,Part006,Part007,open_tin_can001]
  Origin = -> Origin010
